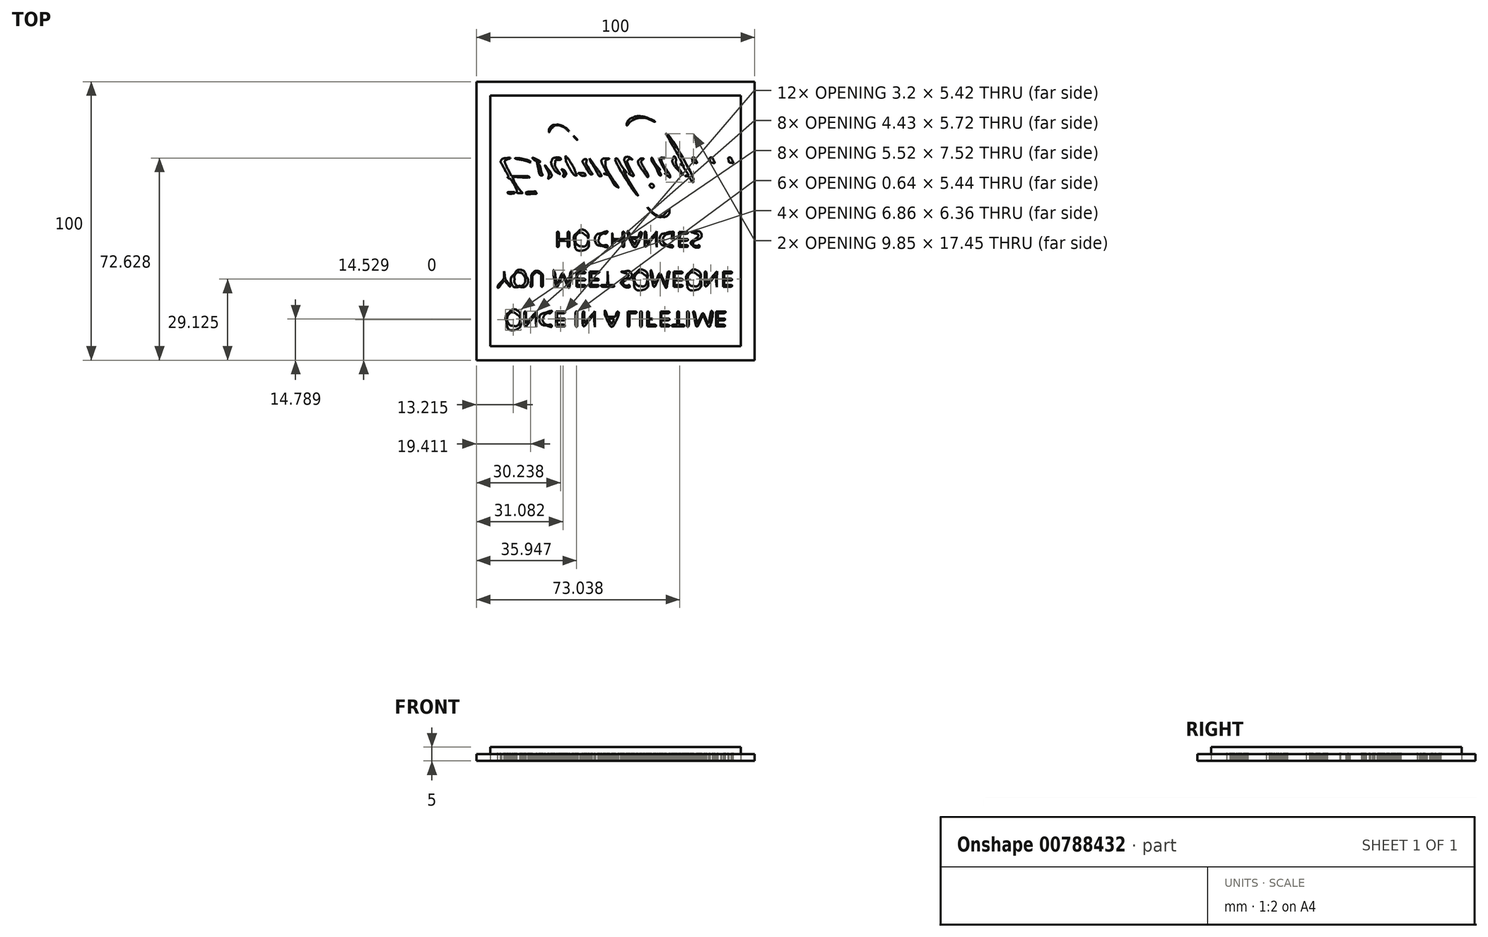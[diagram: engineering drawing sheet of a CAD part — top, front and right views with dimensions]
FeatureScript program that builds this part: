
annotation { "Feature Type Name" : "Feature", "Feature Type Description" : "" }
export const myFeature = defineFeature(function(context is Context, id is Id, definition is map)
    precondition{}
    {
        {
            var Q0;
            Q0=qCreatedBy(makeId("Top.planeOp"),FACE);
            var sketch = newSketch(context, id + "F0", { "sketchPlane" : qUnion([Q0])});
            skLineSegment(sketch, "E0.bottom", {"start": v(50, -50) * mm, "end": v(-50, -50) * mm});
            skLineSegment(sketch, "E0.top", {"start": v(50, 50) * mm, "end": v(-50, 50) * mm});
            skLineSegment(sketch, "E0.left", {"start": v(50, -50) * mm, "end": v(50, 50) * mm});
            skLineSegment(sketch, "E0.right", {"start": v(-50, -50) * mm, "end": v(-50, 50) * mm});
            skPoint(sketch, "E0.middle", {"position": v(0, 0) * mm});
            skSolve(sketch);
        }
        {
            var Q0;
            Q0=makeQuery(id+"F0.imprint","IMPRINT",FACE,{"disambiguationData":[TD([[makeQuery(id+"F0.imprint","IMPRINT",EDGE,{"derivedFrom":sQuery(id+"F0.wireOp",EDGE,"E0.bottom")}),-1.0]])]});
            var sketch = newSketch(context, id + "F1", { "sketchPlane" : qUnion([Q0])});
            skLineSegment(sketch, "E1.bottom", {"start": v(45, -45) * mm, "end": v(-45, -45) * mm});
            skLineSegment(sketch, "E1.top", {"start": v(45, 45) * mm, "end": v(-45, 45) * mm});
            skLineSegment(sketch, "E1.left", {"start": v(45, -45) * mm, "end": v(45, 45) * mm});
            skLineSegment(sketch, "E1.right", {"start": v(-45, -45) * mm, "end": v(-45, 45) * mm});
            skPoint(sketch, "E1.middle", {"position": v(0, 0) * mm});
            skSolve(sketch);
        }
        {
            var Q0;
            Q0 = qSketchRegion(id + "F0", true);
            extrude(context, id + "F2", {"entities" : qUnion([Q0]), "depth" : 2.5 * mm, "offsetDistance" : 25 * mm});
        }
        {
            var Q0;
            Q0 = qSketchRegion(id + "F1", true);
            extrude(context, id + "F3", {"entities" : qUnion([Q0]), "depth" : 5 * mm, "offsetDistance" : 25 * mm});
        }
        {
            var Q0;
            Q0=makeQuery(id+"F2.opExtrude","CAP_FACE",FACE,{"disambiguationData":[OSD([sQuery(id+"F0.wireOp",EDGE,"E0.bottom"),sQuery(id+"F0.wireOp",EDGE,"E0.top"),sQuery(id+"F0.wireOp",EDGE,"E0.left"),sQuery(id+"F0.wireOp",EDGE,"E0.right")])],"isStart":true});
            var sketch = newSketch(context, id + "F4", { "sketchPlane" : qUnion([Q0])});
            skFitSpline(sketch, "E2", {"points": [v(6.09, -37.09) * mm, v(5.28, -36.76) * mm, v(4.06, -35.27) * mm, v(4.06, -34.61) * mm]});
            skFitSpline(sketch, "E3", {"points": [v(4.06, -34.61) * mm, v(4.06, -34.31) * mm, v(4.31, -34.46) * mm, v(4.75, -35.01) * mm]});
            skFitSpline(sketch, "E4", {"points": [v(4.75, -35.01) * mm, v(5.13, -35.5) * mm, v(5.9, -36.08) * mm, v(6.49, -36.33) * mm]});
            skFitSpline(sketch, "E5", {"points": [v(6.49, -36.33) * mm, v(8.03, -36.97) * mm, v(11.26, -36.87) * mm, v(12.9, -36.13) * mm]});
            skFitSpline(sketch, "E6", {"points": [v(12.9, -36.13) * mm, v(13.64, -35.8) * mm, v(14.17, -35.64) * mm, v(14.08, -35.8) * mm]});
            skFitSpline(sketch, "E7", {"points": [v(14.08, -35.8) * mm, v(13.98, -35.96) * mm, v(13.1, -36.38) * mm, v(12.14, -36.74) * mm]});
            skFitSpline(sketch, "E8", {"points": [v(12.14, -36.74) * mm, v(10.33, -37.42) * mm, v(7.34, -37.6) * mm, v(6.09, -37.09) * mm]});
            skFitSpline(sketch, "E9", {"points": [v(15.82, -34.06) * mm, v(16.59, -33.28) * mm, v(17.3, -32.63) * mm, v(17.38, -32.63) * mm]});
            skFitSpline(sketch, "E10", {"points": [v(17.38, -32.63) * mm, v(17.47, -32.63) * mm, v(16.9, -33.28) * mm, v(16.13, -34.06) * mm]});
            skFitSpline(sketch, "E11", {"points": [v(16.13, -34.06) * mm, v(15.36, -34.85) * mm, v(14.66, -35.5) * mm, v(14.57, -35.5) * mm]});
            skFitSpline(sketch, "E12", {"points": [v(14.57, -35.5) * mm, v(14.49, -35.5) * mm, v(15.05, -34.85) * mm, v(15.82, -34.06) * mm]});
            skFitSpline(sketch, "E13", {"points": [v(-23.27, -33.9) * mm, v(-23.62, -33.55) * mm, v(-23.9, -32.95) * mm, v(-23.9, -32.55) * mm]});
            skFitSpline(sketch, "E14", {"points": [v(-23.9, -32.55) * mm, v(-23.88, -31.86) * mm, v(-23.87, -31.86) * mm, v(-23.54, -32.47) * mm]});
            skFitSpline(sketch, "E15", {"points": [v(-23.54, -32.47) * mm, v(-23.35, -32.82) * mm, v(-22.97, -33.29) * mm, v(-22.7, -33.5) * mm]});
            skFitSpline(sketch, "E16", {"points": [v(-22.7, -33.5) * mm, v(-21.6, -34.38) * mm, v(-18.62, -33.71) * mm, v(-16.92, -32.22) * mm]});
            skFitSpline(sketch, "E17", {"points": [v(-16.76, -32.28) * mm, v(-17.58, -33.27) * mm, v(-20.29, -34.53) * mm, v(-21.6, -34.54) * mm]});
            skFitSpline(sketch, "E18", {"points": [v(-21.6, -34.54) * mm, v(-22.21, -34.54) * mm, v(-22.9, -34.28) * mm, v(-23.27, -33.9) * mm]});
            skLineSegment(sketch, "E19", {"start": v(-16.92, -32.22) * mm, "end": v(-16.12, -31.52) * mm});
            skLineSegment(sketch, "E20", {"start": v(-16.12, -31.52) * mm, "end": v(-16.76, -32.28) * mm});
            skLineSegment(sketch, "E21", {"start": v(-16.76, -32.28) * mm, "end": v(-16.92, -32.22) * mm});
            skFitSpline(sketch, "E22", {"points": [v(18.46, -30.69) * mm, v(19.05, -29.76) * mm, v(24.08, -20.5) * mm, v(24.08, -20.32) * mm]});
            skFitSpline(sketch, "E23", {"points": [v(24.08, -20.32) * mm, v(24.08, -20.26) * mm, v(23.91, -20.3) * mm, v(23.71, -20.43) * mm]});
            skFitSpline(sketch, "E24", {"points": [v(23.71, -20.43) * mm, v(23.48, -20.57) * mm, v(23.43, -20.52) * mm, v(23.58, -20.28) * mm]});
            skFitSpline(sketch, "E25", {"points": [v(23.58, -20.28) * mm, v(23.7, -20.08) * mm, v(23.94, -20) * mm, v(24.1, -20.1) * mm]});
            skFitSpline(sketch, "E26", {"points": [v(24.1, -20.1) * mm, v(24.26, -20.2) * mm, v(24.4, -20.05) * mm, v(24.4, -19.76) * mm]});
            skFitSpline(sketch, "E27", {"points": [v(24.4, -19.76) * mm, v(24.4, -19.48) * mm, v(24.75, -18.73) * mm, v(25.2, -18.08) * mm]});
            skFitSpline(sketch, "E28", {"points": [v(25.2, -18.08) * mm, v(26.14, -16.7) * mm, v(26.16, -16.52) * mm, v(25.43, -16.33) * mm]});
            skFitSpline(sketch, "E29", {"points": [v(25.43, -16.33) * mm, v(25, -16.22) * mm, v(25.03, -16.17) * mm, v(25.57, -16.15) * mm]});
            skFitSpline(sketch, "E30", {"points": [v(25.57, -16.15) * mm, v(25.98, -16.12) * mm, v(26.5, -15.72) * mm, v(26.83, -15.16) * mm]});
            skFitSpline(sketch, "E31", {"points": [v(26.83, -15.16) * mm, v(27.43, -14.14) * mm, v(27.9, -13.92) * mm, v(27.9, -14.64) * mm]});
            skFitSpline(sketch, "E32", {"points": [v(27.9, -14.64) * mm, v(27.9, -15.5) * mm, v(19.06, -30.77) * mm, v(18.29, -31.25) * mm]});
            skFitSpline(sketch, "E33", {"points": [v(18.29, -31.25) * mm, v(18.12, -31.35) * mm, v(18.2, -31.1) * mm, v(18.46, -30.69) * mm]});
            skFitSpline(sketch, "E34", {"points": [v(-14.53, -29.77) * mm, v(-14.21, -29.42) * mm, v(-13.88, -29.14) * mm, v(-13.8, -29.14) * mm]});
            skFitSpline(sketch, "E35", {"points": [v(-13.8, -29.14) * mm, v(-13.7, -29.14) * mm, v(-13.9, -29.42) * mm, v(-14.21, -29.77) * mm]});
            skFitSpline(sketch, "E36", {"points": [v(-14.21, -29.77) * mm, v(-14.53, -30.12) * mm, v(-14.86, -30.4) * mm, v(-14.95, -30.4) * mm]});
            skFitSpline(sketch, "E37", {"points": [v(-14.95, -30.4) * mm, v(-15.03, -30.4) * mm, v(-14.85, -30.12) * mm, v(-14.53, -29.77) * mm]});
            skFitSpline(sketch, "E38", {"points": [v(-9.92, -23.1) * mm, v(-9.74, -22.75) * mm, v(-9.51, -22.46) * mm, v(-9.42, -22.46) * mm]});
            skFitSpline(sketch, "E39", {"points": [v(-9.42, -22.46) * mm, v(-9.34, -22.46) * mm, v(-9.42, -22.75) * mm, v(-9.6, -23.1) * mm]});
            skFitSpline(sketch, "E40", {"points": [v(-9.6, -23.1) * mm, v(-9.8, -23.45) * mm, v(-10.02, -23.74) * mm, v(-10.1, -23.74) * mm]});
            skFitSpline(sketch, "E41", {"points": [v(-10.1, -23.74) * mm, v(-10.2, -23.74) * mm, v(-10.1, -23.45) * mm, v(-9.92, -23.1) * mm]});
            skFitSpline(sketch, "E42", {"points": [v(-39.71, -22.55) * mm, v(-40.28, -22.48) * mm, v(-40.88, -22.17) * mm, v(-41.05, -21.86) * mm]});
            skFitSpline(sketch, "E43", {"points": [v(-41.05, -21.86) * mm, v(-41.37, -21.26) * mm, v(-41.32, -21.14) * mm, v(-39.5, -17.95) * mm]});
            skFitSpline(sketch, "E44", {"points": [v(-39.5, -17.95) * mm, v(-38.94, -16.95) * mm, v(-38.55, -16) * mm, v(-38.65, -15.83) * mm]});
            skFitSpline(sketch, "E45", {"points": [v(-38.65, -15.83) * mm, v(-38.75, -15.67) * mm, v(-38.64, -15.46) * mm, v(-38.4, -15.37) * mm]});
            skFitSpline(sketch, "E46", {"points": [v(-38.4, -15.37) * mm, v(-37.92, -15.19) * mm, v(-35.56, -11.12) * mm, v(-35.56, -10.48) * mm]});
            skFitSpline(sketch, "E47", {"points": [v(-35.56, -10.48) * mm, v(-35.56, -10.23) * mm, v(-35.15, -10.07) * mm, v(-34.48, -10.07) * mm]});
            skFitSpline(sketch, "E48", {"points": [v(-34.48, -10.07) * mm, v(-33.44, -10.07) * mm, v(-33.43, -10.09) * mm, v(-33.98, -10.68) * mm]});
            skFitSpline(sketch, "E49", {"points": [v(-33.98, -10.68) * mm, v(-34.63, -11.38) * mm, v(-36.47, -14.37) * mm, v(-36.81, -15.29) * mm]});
            skFitSpline(sketch, "E50", {"points": [v(-36.81, -15.29) * mm, v(-37.03, -15.87) * mm, v(-36.9, -15.88) * mm, v(-33.95, -15.7) * mm]});
            skFitSpline(sketch, "E51", {"points": [v(-33.95, -15.7) * mm, v(-31.98, -15.56) * mm, v(-30.94, -15.6) * mm, v(-31.06, -15.8) * mm]});
            skFitSpline(sketch, "E52", {"points": [v(-31.06, -15.8) * mm, v(-31.16, -15.97) * mm, v(-32.64, -16.1) * mm, v(-34.34, -16.1) * mm]});
            skFitSpline(sketch, "E53", {"points": [v(-38.45, -18.18) * mm, v(-39.52, -20.34) * mm, v(-39.74, -21.63) * mm, v(-39.1, -22.02) * mm]});
            skFitSpline(sketch, "E54", {"points": [v(-39.1, -22.02) * mm, v(-38.9, -22.14) * mm, v(-38.3, -22.35) * mm, v(-37.75, -22.48) * mm]});
            skLineSegment(sketch, "E55", {"start": v(-34.34, -16.1) * mm, "end": v(-37.43, -16.1) * mm});
            skLineSegment(sketch, "E56", {"start": v(-37.43, -16.1) * mm, "end": v(-38.45, -18.18) * mm});
            skLineSegment(sketch, "E57", {"start": v(-38.45, -18.18) * mm, "end": v(-34.34, -16.1) * mm});
            skFitSpline(sketch, "E58", {"points": [v(-37.73, -22.7) * mm, v(-38.25, -22.69) * mm, v(-39.14, -22.62) * mm, v(-39.71, -22.55) * mm]});
            skLineSegment(sketch, "E59", {"start": v(-37.75, -22.48) * mm, "end": v(-36.77, -22.72) * mm});
            skLineSegment(sketch, "E60", {"start": v(-36.77, -22.72) * mm, "end": v(-37.73, -22.7) * mm});
            skLineSegment(sketch, "E61", {"start": v(-37.73, -22.7) * mm, "end": v(-37.75, -22.48) * mm});
            skFitSpline(sketch, "E62", {"points": [v(3.22, -22.3) * mm, v(3.12, -22.04) * mm, v(3.55, -20.75) * mm, v(4.17, -19.44) * mm]});
            skFitSpline(sketch, "E63", {"points": [v(4.17, -19.44) * mm, v(4.86, -17.99) * mm, v(5.15, -17.06) * mm, v(4.92, -17.05) * mm]});
            skFitSpline(sketch, "E64", {"points": [v(4.92, -17.05) * mm, v(4.7, -17.04) * mm, v(4.94, -16.82) * mm, v(5.44, -16.55) * mm]});
            skFitSpline(sketch, "E65", {"points": [v(5.44, -16.55) * mm, v(5.93, -16.28) * mm, v(6.41, -16.13) * mm, v(6.5, -16.22) * mm]});
            skFitSpline(sketch, "E66", {"points": [v(6.5, -16.22) * mm, v(6.59, -16.3) * mm, v(6.3, -17) * mm, v(5.85, -17.75) * mm]});
            skFitSpline(sketch, "E67", {"points": [v(5.85, -17.75) * mm, v(5.4, -18.5) * mm, v(4.83, -19.66) * mm, v(4.56, -20.3) * mm]});
            skFitSpline(sketch, "E68", {"points": [v(4.56, -20.3) * mm, v(4.12, -21.35) * mm, v(4.12, -21.52) * mm, v(4.55, -21.95) * mm]});
            skFitSpline(sketch, "E69", {"points": [v(4.55, -21.95) * mm, v(4.81, -22.22) * mm, v(5.28, -22.36) * mm, v(5.58, -22.26) * mm]});
            skFitSpline(sketch, "E70", {"points": [v(5.58, -22.26) * mm, v(6.04, -22.11) * mm, v(6.05, -22.14) * mm, v(5.65, -22.43) * mm]});
            skFitSpline(sketch, "E71", {"points": [v(5.65, -22.43) * mm, v(4.94, -22.94) * mm, v(3.43, -22.86) * mm, v(3.22, -22.3) * mm]});
            skLineSegment(sketch, "E72", {"start": v(-39.71, -22.55) * mm, "end": v(-39.71, -22.55) * mm});
            skFitSpline(sketch, "E73", {"points": [v(15.93, -22.31) * mm, v(15.83, -22.05) * mm, v(16.34, -20.76) * mm, v(17.06, -19.45) * mm]});
            skFitSpline(sketch, "E74", {"points": [v(17.06, -19.45) * mm, v(17.84, -18.03) * mm, v(18.22, -17.06) * mm, v(17.98, -17.06) * mm]});
            skFitSpline(sketch, "E75", {"points": [v(17.98, -17.06) * mm, v(17.76, -17.06) * mm, v(17.9, -16.84) * mm, v(18.3, -16.56) * mm]});
            skFitSpline(sketch, "E76", {"points": [v(18.3, -16.56) * mm, v(19.58, -15.66) * mm, v(19.6, -16.23) * mm, v(18.34, -18.34) * mm]});
            skFitSpline(sketch, "E77", {"points": [v(18.34, -18.34) * mm, v(16.8, -20.9) * mm, v(16.45, -22.34) * mm, v(17.3, -22.56) * mm]});
            skFitSpline(sketch, "E78", {"points": [v(17.3, -22.56) * mm, v(17.7, -22.66) * mm, v(17.6, -22.72) * mm, v(17, -22.74) * mm]});
            skFitSpline(sketch, "E79", {"points": [v(17, -22.74) * mm, v(16.48, -22.77) * mm, v(16.04, -22.59) * mm, v(15.93, -22.31) * mm]});
            skFitSpline(sketch, "E80", {"points": [v(20.71, -22.34) * mm, v(20.38, -21.49) * mm, v(21.18, -19.8) * mm, v(22.67, -18.16) * mm]});
            skFitSpline(sketch, "E81", {"points": [v(22.67, -18.16) * mm, v(24.2, -16.5) * mm, v(24.2, -16.68) * mm, v(22.68, -18.9) * mm]});
            skFitSpline(sketch, "E82", {"points": [v(22.68, -18.9) * mm, v(22.15, -19.69) * mm, v(21.73, -20.76) * mm, v(21.68, -21.43) * mm]});
            skFitSpline(sketch, "E83", {"points": [v(21.68, -21.43) * mm, v(21.61, -22.65) * mm, v(21.04, -23.19) * mm, v(20.71, -22.34) * mm]});
            skFitSpline(sketch, "E84", {"points": [v(-33.87, -21.99) * mm, v(-32.8, -21.76) * mm, v(-31.44, -21.32) * mm, v(-30.85, -21.03) * mm]});
            skFitSpline(sketch, "E85", {"points": [v(-30.42, -21.15) * mm, v(-30.78, -21.53) * mm, v(-31.8, -21.95) * mm, v(-32.77, -22.14) * mm]});
            skFitSpline(sketch, "E86", {"points": [v(-32.77, -22.14) * mm, v(-35.26, -22.61) * mm, v(-36.16, -22.49) * mm, v(-33.87, -21.99) * mm]});
            skLineSegment(sketch, "E87", {"start": v(-30.85, -21.03) * mm, "end": v(-29.78, -20.5) * mm});
            skLineSegment(sketch, "E88", {"start": v(-29.78, -20.5) * mm, "end": v(-30.42, -21.15) * mm});
            skLineSegment(sketch, "E89", {"start": v(-30.42, -21.15) * mm, "end": v(-30.85, -21.03) * mm});
            skFitSpline(sketch, "E90", {"points": [v(-29.43, -22.14) * mm, v(-29.1, -21.8) * mm, v(-27.08, -21.14) * mm, v(-27.08, -21.37) * mm]});
            skFitSpline(sketch, "E91", {"points": [v(-27.08, -21.37) * mm, v(-27.08, -21.44) * mm, v(-27.5, -21.71) * mm, v(-28.02, -21.98) * mm]});
            skFitSpline(sketch, "E92", {"points": [v(-28.02, -21.98) * mm, v(-29.11, -22.54) * mm, v(-29.92, -22.64) * mm, v(-29.43, -22.14) * mm]});
            skFitSpline(sketch, "E93", {"points": [v(-22.74, -22) * mm, v(-23.14, -20.98) * mm, v(-21.65, -17.9) * mm, v(-20.36, -17.1) * mm]});
            skFitSpline(sketch, "E94", {"points": [v(-20.36, -17.1) * mm, v(-19.94, -16.84) * mm, v(-20, -17.04) * mm, v(-20.59, -17.92) * mm]});
            skFitSpline(sketch, "E95", {"points": [v(-20.59, -17.92) * mm, v(-21.49, -19.25) * mm, v(-21.78, -20.17) * mm, v(-21.63, -21.24) * mm]});
            skFitSpline(sketch, "E96", {"points": [v(-21.63, -21.24) * mm, v(-21.54, -21.84) * mm, v(-21.33, -21.99) * mm, v(-20.52, -21.99) * mm]});
            skFitSpline(sketch, "E97", {"points": [v(-20.52, -21.99) * mm, v(-19.97, -21.99) * mm, v(-19.58, -22.1) * mm, v(-19.66, -22.22) * mm]});
            skFitSpline(sketch, "E98", {"points": [v(-19.66, -22.22) * mm, v(-19.94, -22.68) * mm, v(-22.55, -22.5) * mm, v(-22.74, -22) * mm]});
            skFitSpline(sketch, "E99", {"points": [v(-17.85, -22.23) * mm, v(-17.8, -21.54) * mm, v(-14.72, -16.43) * mm, v(-14.35, -16.43) * mm]});
            skFitSpline(sketch, "E100", {"points": [v(-14.35, -16.43) * mm, v(-13.97, -16.43) * mm, v(-13.98, -16.5) * mm, v(-14.45, -17.58) * mm]});
            skFitSpline(sketch, "E101", {"points": [v(-14.45, -17.58) * mm, v(-15.5, -19.98) * mm, v(-17.92, -23.29) * mm, v(-17.85, -22.23) * mm]});
            skFitSpline(sketch, "E102", {"points": [v(-4.63, -22.25) * mm, v(-5.07, -21.8) * mm, v(-4.8, -20.56) * mm, v(-3.9, -18.84) * mm]});
            skFitSpline(sketch, "E103", {"points": [v(-3.9, -18.84) * mm, v(-2.97, -17.08) * mm, v(-2.97, -17.06) * mm, v(-3.66, -17.03) * mm]});
            skFitSpline(sketch, "E104", {"points": [v(-3.66, -17.03) * mm, v(-4.22, -17.01) * mm, v(-4.17, -16.95) * mm, v(-3.4, -16.72) * mm]});
            skFitSpline(sketch, "E105", {"points": [v(-3.4, -16.72) * mm, v(-2.7, -16.51) * mm, v(-2.17, -15.94) * mm, v(-1.38, -14.56) * mm]});
            skFitSpline(sketch, "E106", {"points": [v(-1.38, -14.56) * mm, v(-0.78, -13.52) * mm, v(0.04, -12.52) * mm, v(0.44, -12.34) * mm]});
            skFitSpline(sketch, "E107", {"points": [v(0.44, -12.34) * mm, v(1.12, -12.03) * mm, v(1.1, -12.13) * mm, v(0.12, -13.5) * mm]});
            skFitSpline(sketch, "E108", {"points": [v(0.12, -13.5) * mm, v(-1.72, -16.1) * mm, v(-3.57, -19.76) * mm, v(-3.57, -20.83) * mm]});
            skFitSpline(sketch, "E109", {"points": [v(-3.57, -20.83) * mm, v(-3.57, -21.59) * mm, v(-3.38, -21.92) * mm, v(-2.85, -22.14) * mm]});
            skFitSpline(sketch, "E110", {"points": [v(-2.85, -22.14) * mm, v(-2.22, -22.39) * mm, v(-2.27, -22.43) * mm, v(-3.28, -22.44) * mm]});
            skFitSpline(sketch, "E111", {"points": [v(-3.28, -22.44) * mm, v(-3.9, -22.45) * mm, v(-4.5, -22.37) * mm, v(-4.63, -22.25) * mm]});
            skFitSpline(sketch, "E112", {"points": [v(-0.07, -22.28) * mm, v(-0.07, -21.75) * mm, v(7.4, -9.56) * mm, v(7.93, -9.24) * mm]});
            skFitSpline(sketch, "E113", {"points": [v(7.93, -9.24) * mm, v(8.09, -9.14) * mm, v(7.73, -9.83) * mm, v(7.13, -10.76) * mm]});
            skFitSpline(sketch, "E114", {"points": [v(7.13, -10.76) * mm, v(5.14, -13.88) * mm, v(2.94, -18.2) * mm, v(3.6, -17.7) * mm]});
            skFitSpline(sketch, "E115", {"points": [v(3.6, -17.7) * mm, v(3.94, -17.44) * mm, v(3.79, -17.72) * mm, v(3.27, -18.34) * mm]});
            skFitSpline(sketch, "E116", {"points": [v(3.27, -18.34) * mm, v(2.74, -18.95) * mm, v(1.95, -20.13) * mm, v(1.52, -20.96) * mm]});
            skFitSpline(sketch, "E117", {"points": [v(1.52, -20.96) * mm, v(1.08, -21.79) * mm, v(0.55, -22.46) * mm, v(0.33, -22.46) * mm]});
            skFitSpline(sketch, "E118", {"points": [v(0.33, -22.46) * mm, v(0.1, -22.46) * mm, v(-0.07, -22.38) * mm, v(-0.07, -22.28) * mm]});
            skLineSegment(sketch, "E119", {"start": v(-4.63, -22.25) * mm, "end": v(-4.63, -22.25) * mm});
            skFitSpline(sketch, "E120", {"points": [v(8.52, -22) * mm, v(8.08, -21.47) * mm, v(8.95, -19.23) * mm, v(10.28, -17.48) * mm]});
            skFitSpline(sketch, "E121", {"points": [v(10.28, -17.48) * mm, v(11.6, -15.75) * mm, v(11.75, -16.28) * mm, v(10.57, -18.44) * mm]});
            skFitSpline(sketch, "E122", {"points": [v(10.57, -18.44) * mm, v(9.4, -20.57) * mm, v(9.22, -21.46) * mm, v(9.84, -22.08) * mm]});
            skFitSpline(sketch, "E123", {"points": [v(9.84, -22.08) * mm, v(10.14, -22.38) * mm, v(10.08, -22.46) * mm, v(9.56, -22.46) * mm]});
            skFitSpline(sketch, "E124", {"points": [v(9.56, -22.46) * mm, v(9.2, -22.46) * mm, v(8.73, -22.26) * mm, v(8.52, -22) * mm]});
            skFitSpline(sketch, "E125", {"points": [v(12.96, -22) * mm, v(12.96, -21.75) * mm, v(13.3, -21.03) * mm, v(13.72, -20.42) * mm]});
            skFitSpline(sketch, "E126", {"points": [v(13.72, -20.42) * mm, v(14.14, -19.8) * mm, v(14.74, -18.65) * mm, v(15.07, -17.86) * mm]});
            skFitSpline(sketch, "E127", {"points": [v(15.07, -17.86) * mm, v(15.4, -17.07) * mm, v(15.84, -16.43) * mm, v(16.06, -16.43) * mm]});
            skFitSpline(sketch, "E128", {"points": [v(16.06, -16.43) * mm, v(16.34, -16.43) * mm, v(16.26, -16.83) * mm, v(15.78, -17.77) * mm]});
            skFitSpline(sketch, "E129", {"points": [v(15.78, -17.77) * mm, v(15.15, -19) * mm, v(15.14, -19.08) * mm, v(15.7, -18.65) * mm]});
            skFitSpline(sketch, "E130", {"points": [v(15.7, -18.65) * mm, v(16.02, -18.39) * mm, v(15.83, -18.71) * mm, v(15.27, -19.37) * mm]});
            skFitSpline(sketch, "E131", {"points": [v(15.27, -19.37) * mm, v(14.7, -20.03) * mm, v(14.02, -21) * mm, v(13.75, -21.51) * mm]});
            skFitSpline(sketch, "E132", {"points": [v(13.75, -21.51) * mm, v(13.21, -22.56) * mm, v(12.96, -22.71) * mm, v(12.96, -22) * mm]});
            skFitSpline(sketch, "E133", {"points": [v(27.63, -21.75) * mm, v(27.7, -21.29) * mm, v(27.99, -21) * mm, v(28.45, -20.93) * mm]});
            skFitSpline(sketch, "E134", {"points": [v(28.45, -20.93) * mm, v(29.25, -20.82) * mm, v(29.3, -20.96) * mm, v(28.83, -21.85) * mm]});
            skFitSpline(sketch, "E135", {"points": [v(28.83, -21.85) * mm, v(28.37, -22.72) * mm, v(27.5, -22.65) * mm, v(27.63, -21.75) * mm]});
            skFitSpline(sketch, "E136", {"points": [v(33.99, -21.75) * mm, v(34.05, -21.29) * mm, v(34.34, -21) * mm, v(34.8, -20.93) * mm]});
            skFitSpline(sketch, "E137", {"points": [v(34.8, -20.93) * mm, v(35.6, -20.82) * mm, v(35.67, -20.96) * mm, v(35.19, -21.85) * mm]});
            skFitSpline(sketch, "E138", {"points": [v(35.19, -21.85) * mm, v(34.72, -22.72) * mm, v(33.86, -22.65) * mm, v(33.99, -21.75) * mm]});
            skFitSpline(sketch, "E139", {"points": [v(40.66, -21.75) * mm, v(40.73, -21.29) * mm, v(41.02, -21) * mm, v(41.48, -20.93) * mm]});
            skFitSpline(sketch, "E140", {"points": [v(41.48, -20.93) * mm, v(42.28, -20.82) * mm, v(42.34, -20.96) * mm, v(41.86, -21.85) * mm]});
            skFitSpline(sketch, "E141", {"points": [v(41.86, -21.85) * mm, v(41.4, -22.72) * mm, v(40.53, -22.65) * mm, v(40.66, -21.75) * mm]});
            skFitSpline(sketch, "E142", {"points": [v(-11.65, -21.86) * mm, v(-11.9, -21.45) * mm, v(-11.59, -20.68) * mm, v(-10.3, -18.57) * mm]});
            skFitSpline(sketch, "E143", {"points": [v(-10.3, -18.57) * mm, v(-9.7, -17.57) * mm, v(-9, -16.74) * mm, v(-8.74, -16.74) * mm]});
            skFitSpline(sketch, "E144", {"points": [v(-8.74, -16.74) * mm, v(-8.29, -16.74) * mm, v(-8.5, -17.18) * mm, v(-10.18, -19.84) * mm]});
            skFitSpline(sketch, "E145", {"points": [v(-10.18, -19.84) * mm, v(-10.43, -20.24) * mm, v(-10.56, -20.92) * mm, v(-10.48, -21.35) * mm]});
            skFitSpline(sketch, "E146", {"points": [v(-10.48, -21.35) * mm, v(-10.36, -21.96) * mm, v(-10.46, -22.15) * mm, v(-10.9, -22.15) * mm]});
            skFitSpline(sketch, "E147", {"points": [v(-10.9, -22.15) * mm, v(-11.22, -22.15) * mm, v(-11.55, -22.02) * mm, v(-11.65, -21.86) * mm]});
            skFitSpline(sketch, "E148", {"points": [v(-9.1, -21.67) * mm, v(-8.97, -21.32) * mm, v(-8.7, -20.82) * mm, v(-8.5, -20.56) * mm]});
            skFitSpline(sketch, "E149", {"points": [v(-8.5, -20.56) * mm, v(-8.28, -20.3) * mm, v(-7.63, -19.19) * mm, v(-7.04, -18.1) * mm]});
            skFitSpline(sketch, "E150", {"points": [v(-7.04, -18.1) * mm, v(-6.45, -17) * mm, v(-5.85, -16.1) * mm, v(-5.72, -16.1) * mm]});
            skFitSpline(sketch, "E151", {"points": [v(-5.72, -16.1) * mm, v(-5.1, -16.1) * mm, v(-5.61, -17.34) * mm, v(-7.12, -19.4) * mm]});
            skFitSpline(sketch, "E152", {"points": [v(-7.12, -19.4) * mm, v(-9.17, -22.23) * mm, v(-9.38, -22.47) * mm, v(-9.1, -21.67) * mm]});
            skFitSpline(sketch, "E153", {"points": [v(-27.84, -19.14) * mm, v(-27.42, -17.13) * mm, v(-27.05, -16.44) * mm, v(-26.36, -16.43) * mm]});
            skFitSpline(sketch, "E154", {"points": [v(-26.36, -16.43) * mm, v(-26.22, -16.43) * mm, v(-26.24, -16.68) * mm, v(-26.4, -16.98) * mm]});
            skFitSpline(sketch, "E155", {"points": [v(-26.4, -16.98) * mm, v(-26.55, -17.29) * mm, v(-26.78, -18.06) * mm, v(-26.9, -18.7) * mm]});
            skFitSpline(sketch, "E156", {"points": [v(-26.9, -18.7) * mm, v(-27, -19.35) * mm, v(-27.37, -20.2) * mm, v(-27.7, -20.61) * mm]});
            skFitSpline(sketch, "E157", {"points": [v(-27.7, -20.61) * mm, v(-28.3, -21.34) * mm, v(-28.3, -21.32) * mm, v(-27.84, -19.14) * mm]});
            skFitSpline(sketch, "E158", {"points": [v(-24.64, -18.41) * mm, v(-24.12, -17.4) * mm, v(-23.92, -16.6) * mm, v(-24.04, -16) * mm]});
            skFitSpline(sketch, "E159", {"points": [v(-24.04, -16) * mm, v(-24.2, -15.2) * mm, v(-24.15, -15.13) * mm, v(-23.74, -15.47) * mm]});
            skFitSpline(sketch, "E160", {"points": [v(-23.74, -15.47) * mm, v(-23.01, -16.08) * mm, v(-23.18, -17.16) * mm, v(-24.22, -18.6) * mm]});
            skFitSpline(sketch, "E161", {"points": [v(-24.22, -18.6) * mm, v(-24.75, -19.33) * mm, v(-25.23, -19.92) * mm, v(-25.3, -19.92) * mm]});
            skFitSpline(sketch, "E162", {"points": [v(-25.3, -19.92) * mm, v(-25.36, -19.92) * mm, v(-25.06, -19.24) * mm, v(-24.64, -18.41) * mm]});
            skFitSpline(sketch, "E163", {"points": [v(-18.97, -17.9) * mm, v(-18.7, -17.48) * mm, v(-18.58, -16.92) * mm, v(-18.69, -16.63) * mm]});
            skFitSpline(sketch, "E164", {"points": [v(-18.69, -16.63) * mm, v(-18.9, -16.05) * mm, v(-18.35, -15.9) * mm, v(-18, -16.46) * mm]});
            skFitSpline(sketch, "E165", {"points": [v(-18, -16.46) * mm, v(-17.74, -16.88) * mm, v(-18.43, -18.24) * mm, v(-19.02, -18.47) * mm]});
            skFitSpline(sketch, "E166", {"points": [v(-19.02, -18.47) * mm, v(-19.36, -18.6) * mm, v(-19.35, -18.47) * mm, v(-18.97, -17.9) * mm]});
            skFitSpline(sketch, "E167", {"points": [v(-12.89, -16.82) * mm, v(-12.17, -16.3) * mm, v(-10.78, -16.3) * mm, v(-10.95, -16.82) * mm]});
            skFitSpline(sketch, "E168", {"points": [v(-10.95, -16.82) * mm, v(-11.03, -17.04) * mm, v(-11.61, -17.22) * mm, v(-12.26, -17.22) * mm]});
            skFitSpline(sketch, "E169", {"points": [v(-12.26, -17.22) * mm, v(-13.27, -17.22) * mm, v(-13.36, -17.17) * mm, v(-12.89, -16.82) * mm]});
            skFitSpline(sketch, "E170", {"points": [v(12.32, -12.97) * mm, v(12.32, -12.57) * mm, v(13.25, -11.85) * mm, v(13.48, -12.08) * mm]});
            skFitSpline(sketch, "E171", {"points": [v(13.48, -12.08) * mm, v(13.8, -12.4) * mm, v(13.32, -13.25) * mm, v(12.8, -13.25) * mm]});
            skFitSpline(sketch, "E172", {"points": [v(12.8, -13.25) * mm, v(12.54, -13.25) * mm, v(12.32, -13.12) * mm, v(12.32, -12.97) * mm]});
            skLineSegment(sketch, "E173", {"start": v(-12.89, -16.82) * mm, "end": v(-12.89, -16.82) * mm});
            skFitSpline(sketch, "E174", {"points": [v(-30.26, -10.47) * mm, v(-32.18, -10.25) * mm, v(-32.12, -9.75) * mm, v(-30.17, -9.75) * mm]});
            skFitSpline(sketch, "E175", {"points": [v(-30.17, -9.75) * mm, v(-28.7, -9.75) * mm, v(-28.4, -9.84) * mm, v(-28.56, -10.23) * mm]});
            skFitSpline(sketch, "E176", {"points": [v(-28.56, -10.23) * mm, v(-28.66, -10.5) * mm, v(-28.83, -10.68) * mm, v(-28.94, -10.66) * mm]});
            skFitSpline(sketch, "E177", {"points": [v(-28.94, -10.66) * mm, v(-29.06, -10.63) * mm, v(-29.65, -10.55) * mm, v(-30.26, -10.47) * mm]});
            skFitSpline(sketch, "E178", {"points": [v(-38.72, -10.13) * mm, v(-38.57, -9.89) * mm, v(-36.3, -10.01) * mm, v(-36.3, -10.26) * mm]});
            skFitSpline(sketch, "E179", {"points": [v(-36.3, -10.26) * mm, v(-36.3, -10.33) * mm, v(-36.88, -10.39) * mm, v(-37.59, -10.39) * mm]});
            skFitSpline(sketch, "E180", {"points": [v(-37.59, -10.39) * mm, v(-38.3, -10.39) * mm, v(-38.8, -10.27) * mm, v(-38.72, -10.13) * mm]});
            skFitSpline(sketch, "E181", {"points": [v(11.53, -4.7) * mm, v(13.5, -2.61) * mm, v(15.34, -1.51) * mm, v(16.86, -1.5) * mm]});
            skFitSpline(sketch, "E182", {"points": [v(16.86, -1.5) * mm, v(17.9, -1.5) * mm, v(19.31, -2.75) * mm, v(19.31, -3.68) * mm]});
            skFitSpline(sketch, "E183", {"points": [v(19.31, -3.68) * mm, v(19.31, -4.23) * mm, v(19.2, -4.2) * mm, v(18.38, -3.37) * mm]});
            skFitSpline(sketch, "E184", {"points": [v(18.38, -3.37) * mm, v(16.77, -1.76) * mm, v(14.38, -2.3) * mm, v(11.55, -4.93) * mm]});
            skFitSpline(sketch, "E185", {"points": [v(-28.51, 4.3) * mm, v(-28.59, 4.53) * mm, v(-29, 5.67) * mm, v(-29.42, 6.85) * mm]});
            skFitSpline(sketch, "E186", {"points": [v(-29.42, 6.85) * mm, v(-29.84, 8.04) * mm, v(-30.06, 9.08) * mm, v(-29.9, 9.18) * mm]});
            skFitSpline(sketch, "E187", {"points": [v(-29.9, 9.18) * mm, v(-29.6, 9.36) * mm, v(-29.32, 8.74) * mm, v(-28.65, 6.51) * mm]});
            skFitSpline(sketch, "E188", {"points": [v(-28.65, 6.51) * mm, v(-28.43, 5.78) * mm, v(-28.17, 5.18) * mm, v(-28.06, 5.18) * mm]});
            skFitSpline(sketch, "E189", {"points": [v(-28.06, 5.18) * mm, v(-27.96, 5.18) * mm, v(-27.58, 6) * mm, v(-27.22, 6.99) * mm]});
            skFitSpline(sketch, "E190", {"points": [v(-27.22, 6.99) * mm, v(-26.87, 7.98) * mm, v(-26.42, 8.85) * mm, v(-26.22, 8.91) * mm]});
            skFitSpline(sketch, "E191", {"points": [v(-26.22, 8.91) * mm, v(-26.03, 8.97) * mm, v(-25.63, 8.27) * mm, v(-25.33, 7.34) * mm]});
            skFitSpline(sketch, "E192", {"points": [v(-25.33, 7.34) * mm, v(-25.03, 6.42) * mm, v(-24.67, 5.54) * mm, v(-24.54, 5.4) * mm]});
            skFitSpline(sketch, "E193", {"points": [v(-24.54, 5.4) * mm, v(-24.4, 5.25) * mm, v(-23.98, 6.07) * mm, v(-23.6, 7.22) * mm]});
            skFitSpline(sketch, "E194", {"points": [v(-23.6, 7.22) * mm, v(-23.21, 8.37) * mm, v(-22.77, 9.31) * mm, v(-22.6, 9.31) * mm]});
            skFitSpline(sketch, "E195", {"points": [v(-22.6, 9.31) * mm, v(-22.22, 9.31) * mm, v(-22.19, 9.47) * mm, v(-23.23, 6.6) * mm]});
            skFitSpline(sketch, "E196", {"points": [v(-23.23, 6.6) * mm, v(-23.73, 5.23) * mm, v(-24.28, 4.05) * mm, v(-24.45, 4) * mm]});
            skFitSpline(sketch, "E197", {"points": [v(-24.45, 4) * mm, v(-24.62, 3.94) * mm, v(-25.01, 4.76) * mm, v(-25.34, 5.82) * mm]});
            skFitSpline(sketch, "E198", {"points": [v(-25.34, 5.82) * mm, v(-25.66, 6.89) * mm, v(-26.03, 7.82) * mm, v(-26.15, 7.9) * mm]});
            skFitSpline(sketch, "E199", {"points": [v(-26.15, 7.9) * mm, v(-26.28, 7.98) * mm, v(-26.72, 7.11) * mm, v(-27.13, 5.98) * mm]});
            skFitSpline(sketch, "E200", {"points": [v(-27.13, 5.98) * mm, v(-27.85, 3.96) * mm, v(-28.23, 3.5) * mm, v(-28.51, 4.3) * mm]});
            skLineSegment(sketch, "E201", {"start": v(11.55, -4.93) * mm, "end": v(9.62, -6.71) * mm});
            skLineSegment(sketch, "E202", {"start": v(9.62, -6.71) * mm, "end": v(11.53, -4.7) * mm});
            skLineSegment(sketch, "E203", {"start": v(11.53, -4.7) * mm, "end": v(11.55, -4.93) * mm});
            skFitSpline(sketch, "E204", {"points": [v(-21.04, 6.61) * mm, v(-21.04, 8.2) * mm, v(-20.91, 9.31) * mm, v(-20.73, 9.31) * mm]});
            skFitSpline(sketch, "E205", {"points": [v(-20.73, 9.31) * mm, v(-20.55, 9.31) * mm, v(-20.4, 8.81) * mm, v(-20.4, 8.2) * mm]});
            skFitSpline(sketch, "E206", {"points": [v(-17.23, 8.2) * mm, v(-17.23, 8.81) * mm, v(-17.09, 9.31) * mm, v(-16.91, 9.31) * mm]});
            skFitSpline(sketch, "E207", {"points": [v(-16.91, 9.31) * mm, v(-16.73, 9.31) * mm, v(-16.6, 8.2) * mm, v(-16.6, 6.61) * mm]});
            skFitSpline(sketch, "E208", {"points": [v(-16.6, 6.61) * mm, v(-16.6, 5.02) * mm, v(-16.73, 3.91) * mm, v(-16.91, 3.91) * mm]});
            skFitSpline(sketch, "E209", {"points": [v(-16.91, 3.91) * mm, v(-17.09, 3.91) * mm, v(-17.23, 4.48) * mm, v(-17.23, 5.18) * mm]});
            skLineSegment(sketch, "E210", {"start": v(-20.4, 8.2) * mm, "end": v(-20.4, 7.09) * mm});
            skLineSegment(sketch, "E211", {"start": v(-20.4, 7.09) * mm, "end": v(-18.82, 7.09) * mm});
            skLineSegment(sketch, "E212", {"start": v(-18.82, 7.09) * mm, "end": v(-17.23, 7.09) * mm});
            skLineSegment(sketch, "E213", {"start": v(-17.23, 7.09) * mm, "end": v(-17.23, 8.2) * mm});
            skLineSegment(sketch, "E214", {"start": v(-17.23, 8.2) * mm, "end": v(-20.4, 8.2) * mm});
            skFitSpline(sketch, "E215", {"points": [v(-20.4, 5.18) * mm, v(-20.4, 4.48) * mm, v(-20.55, 3.91) * mm, v(-20.73, 3.91) * mm]});
            skFitSpline(sketch, "E216", {"points": [v(-20.73, 3.91) * mm, v(-20.91, 3.91) * mm, v(-21.04, 5.02) * mm, v(-21.04, 6.61) * mm]});
            skLineSegment(sketch, "E217", {"start": v(-17.23, 5.18) * mm, "end": v(-17.23, 6.45) * mm});
            skLineSegment(sketch, "E218", {"start": v(-17.23, 6.45) * mm, "end": v(-18.82, 6.45) * mm});
            skLineSegment(sketch, "E219", {"start": v(-18.82, 6.45) * mm, "end": v(-20.4, 6.45) * mm});
            skLineSegment(sketch, "E220", {"start": v(-20.4, 6.45) * mm, "end": v(-20.4, 5.18) * mm});
            skLineSegment(sketch, "E221", {"start": v(-20.4, 5.18) * mm, "end": v(-17.23, 5.18) * mm});
            skFitSpline(sketch, "E222", {"points": [v(-13.82, 4.3) * mm, v(-14.7, 4.98) * mm, v(-15.07, 6.4) * mm, v(-14.67, 7.61) * mm]});
            skFitSpline(sketch, "E223", {"points": [v(-14.67, 7.61) * mm, v(-13.73, 10.47) * mm, v(-9.92, 9.64) * mm, v(-9.92, 6.57) * mm]});
            skFitSpline(sketch, "E224", {"points": [v(-9.92, 6.57) * mm, v(-9.92, 4.44) * mm, v(-12.23, 3.1) * mm, v(-13.82, 4.3) * mm]});
            skFitSpline(sketch, "E225", {"points": [v(-11.2, 4.86) * mm, v(-9.9, 6.16) * mm, v(-10.76, 9) * mm, v(-12.44, 9) * mm]});
            skFitSpline(sketch, "E226", {"points": [v(-12.44, 9) * mm, v(-13.2, 9) * mm, v(-14.37, 7.56) * mm, v(-14.37, 6.61) * mm]});
            skFitSpline(sketch, "E227", {"points": [v(-14.37, 6.61) * mm, v(-14.37, 5.67) * mm, v(-13.2, 4.23) * mm, v(-12.44, 4.23) * mm]});
            skFitSpline(sketch, "E228", {"points": [v(-12.44, 4.23) * mm, v(-12.1, 4.23) * mm, v(-11.54, 4.51) * mm, v(-11.2, 4.86) * mm]});
            skFitSpline(sketch, "E229", {"points": [v(-5.03, 4.37) * mm, v(-7.08, 5.26) * mm, v(-6.95, 8.21) * mm, v(-4.82, 8.95) * mm]});
            skFitSpline(sketch, "E230", {"points": [v(-4.82, 8.95) * mm, v(-3.55, 9.4) * mm, v(-2.93, 9.41) * mm, v(-2.93, 9) * mm]});
            skFitSpline(sketch, "E231", {"points": [v(-2.93, 9) * mm, v(-2.93, 8.82) * mm, v(-3.3, 8.68) * mm, v(-3.74, 8.68) * mm]});
            skFitSpline(sketch, "E232", {"points": [v(-3.74, 8.68) * mm, v(-4.88, 8.68) * mm, v(-6.2, 7.28) * mm, v(-5.94, 6.37) * mm]});
            skFitSpline(sketch, "E233", {"points": [v(-5.94, 6.37) * mm, v(-5.68, 5.47) * mm, v(-4.63, 4.55) * mm, v(-3.87, 4.55) * mm]});
            skFitSpline(sketch, "E234", {"points": [v(-3.87, 4.55) * mm, v(-3.55, 4.55) * mm, v(-3.2, 4.4) * mm, v(-3.1, 4.23) * mm]});
            skFitSpline(sketch, "E235", {"points": [v(-3.1, 4.23) * mm, v(-2.81, 3.78) * mm, v(-3.86, 3.86) * mm, v(-5.03, 4.37) * mm]});
            skFitSpline(sketch, "E236", {"points": [v(-1.23, 6.61) * mm, v(-1.23, 8.18) * mm, v(-1.18, 8.94) * mm, v(-1.11, 8.28) * mm]});
            skFitSpline(sketch, "E237", {"points": [v(2.47, 8.2) * mm, v(2.47, 8.81) * mm, v(2.61, 9.31) * mm, v(2.79, 9.31) * mm]});
            skFitSpline(sketch, "E238", {"points": [v(2.79, 9.31) * mm, v(2.98, 9.31) * mm, v(3.1, 8.2) * mm, v(3.1, 6.61) * mm]});
            skFitSpline(sketch, "E239", {"points": [v(3.1, 6.61) * mm, v(3.1, 5.02) * mm, v(2.98, 3.91) * mm, v(2.79, 3.91) * mm]});
            skFitSpline(sketch, "E240", {"points": [v(2.79, 3.91) * mm, v(2.61, 3.91) * mm, v(2.47, 4.48) * mm, v(2.47, 5.18) * mm]});
            skLineSegment(sketch, "E241", {"start": v(-1.11, 8.28) * mm, "end": v(-0.99, 7.09) * mm});
            skLineSegment(sketch, "E242", {"start": v(-0.99, 7.09) * mm, "end": v(0.74, 7.09) * mm});
            skLineSegment(sketch, "E243", {"start": v(0.74, 7.09) * mm, "end": v(2.47, 7.09) * mm});
            skLineSegment(sketch, "E244", {"start": v(2.47, 7.09) * mm, "end": v(2.47, 8.2) * mm});
            skLineSegment(sketch, "E245", {"start": v(2.47, 8.2) * mm, "end": v(-1.11, 8.28) * mm});
            skFitSpline(sketch, "E246", {"points": [v(-1.1, 5.1) * mm, v(-1.18, 4.36) * mm, v(-1.23, 5.04) * mm, v(-1.23, 6.61) * mm]});
            skLineSegment(sketch, "E247", {"start": v(2.47, 5.18) * mm, "end": v(2.47, 6.45) * mm});
            skLineSegment(sketch, "E248", {"start": v(2.47, 6.45) * mm, "end": v(0.74, 6.45) * mm});
            skLineSegment(sketch, "E249", {"start": v(0.74, 6.45) * mm, "end": v(-0.99, 6.45) * mm});
            skLineSegment(sketch, "E250", {"start": v(-0.99, 6.45) * mm, "end": v(-1.1, 5.1) * mm});
            skLineSegment(sketch, "E251", {"start": v(-1.1, 5.1) * mm, "end": v(2.47, 5.18) * mm});
            skFitSpline(sketch, "E252", {"points": [v(4.38, 4.21) * mm, v(4.38, 4.77) * mm, v(6.56, 9.31) * mm, v(6.83, 9.31) * mm]});
            skFitSpline(sketch, "E253", {"points": [v(6.83, 9.31) * mm, v(7.25, 9.31) * mm, v(9.44, 4.25) * mm, v(9.1, 4.05) * mm]});
            skFitSpline(sketch, "E254", {"points": [v(9.1, 4.05) * mm, v(8.94, 3.95) * mm, v(8.66, 4.3) * mm, v(8.47, 4.84) * mm]});
            skFitSpline(sketch, "E255", {"points": [v(8.47, 4.84) * mm, v(8.16, 5.73) * mm, v(8, 5.82) * mm, v(6.76, 5.82) * mm]});
            skFitSpline(sketch, "E256", {"points": [v(6.76, 5.82) * mm, v(5.53, 5.82) * mm, v(5.36, 5.72) * mm, v(5.06, 4.86) * mm]});
            skFitSpline(sketch, "E257", {"points": [v(5.06, 4.86) * mm, v(4.74, 3.94) * mm, v(4.38, 3.6) * mm, v(4.38, 4.21) * mm]});
            skFitSpline(sketch, "E258", {"points": [v(7.56, 6.8) * mm, v(7.56, 6.98) * mm, v(7.4, 7.43) * mm, v(7.2, 7.8) * mm]});
            skFitSpline(sketch, "E259", {"points": [v(7.2, 7.8) * mm, v(6.84, 8.47) * mm, v(6.84, 8.47) * mm, v(6.41, 7.7) * mm]});
            skFitSpline(sketch, "E260", {"points": [v(6.41, 7.7) * mm, v(5.81, 6.62) * mm, v(5.86, 6.45) * mm, v(6.76, 6.45) * mm]});
            skFitSpline(sketch, "E261", {"points": [v(6.76, 6.45) * mm, v(7.2, 6.45) * mm, v(7.56, 6.6) * mm, v(7.56, 6.8) * mm]});
            skFitSpline(sketch, "E262", {"points": [v(10.42, 6.43) * mm, v(10.42, 7.82) * mm, v(10.55, 9.04) * mm, v(10.7, 9.14) * mm]});
            skFitSpline(sketch, "E263", {"points": [v(10.7, 9.14) * mm, v(10.86, 9.23) * mm, v(11.76, 8.35) * mm, v(12.7, 7.18) * mm]});
            skFitSpline(sketch, "E264", {"points": [v(14.14, 4.57) * mm, v(13.75, 5.01) * mm, v(12.9, 6.01) * mm, v(12.26, 6.79) * mm]});
            skLineSegment(sketch, "E265", {"start": v(12.7, 7.18) * mm, "end": v(14.39, 5.04) * mm});
            skLineSegment(sketch, "E266", {"start": v(14.39, 5.04) * mm, "end": v(14.57, 7.26) * mm});
            skLineSegment(sketch, "E267", {"start": v(14.57, 7.26) * mm, "end": v(14.75, 9.47) * mm});
            skLineSegment(sketch, "E268", {"start": v(14.75, 9.47) * mm, "end": v(14.8, 6.61) * mm});
            skLineSegment(sketch, "E269", {"start": v(14.8, 6.61) * mm, "end": v(14.84, 3.75) * mm});
            skLineSegment(sketch, "E270", {"start": v(14.84, 3.75) * mm, "end": v(14.14, 4.57) * mm});
            skLineSegment(sketch, "E271", {"start": v(14.14, 4.57) * mm, "end": v(12.7, 7.18) * mm});
            skFitSpline(sketch, "E272", {"points": [v(11.06, 6.06) * mm, v(11.06, 4.85) * mm, v(10.91, 3.91) * mm, v(10.73, 3.91) * mm]});
            skFitSpline(sketch, "E273", {"points": [v(10.73, 3.91) * mm, v(10.55, 3.91) * mm, v(10.42, 4.96) * mm, v(10.42, 6.43) * mm]});
            skLineSegment(sketch, "E274", {"start": v(12.26, 6.79) * mm, "end": v(11.08, 8.2) * mm});
            skLineSegment(sketch, "E275", {"start": v(11.08, 8.2) * mm, "end": v(11.06, 6.06) * mm});
            skLineSegment(sketch, "E276", {"start": v(11.06, 6.06) * mm, "end": v(12.26, 6.79) * mm});
            skFitSpline(sketch, "E277", {"points": [v(18.16, 4.37) * mm, v(16.12, 5.26) * mm, v(16.25, 8.21) * mm, v(18.37, 8.95) * mm]});
            skFitSpline(sketch, "E278", {"points": [v(18.37, 8.95) * mm, v(19.65, 9.4) * mm, v(20.58, 9.42) * mm, v(20.58, 9) * mm]});
            skFitSpline(sketch, "E279", {"points": [v(20.58, 9) * mm, v(20.58, 8.82) * mm, v(20.15, 8.68) * mm, v(19.62, 8.68) * mm]});
            skFitSpline(sketch, "E280", {"points": [v(19.62, 8.68) * mm, v(18.59, 8.68) * mm, v(17.09, 7.48) * mm, v(17.09, 6.66) * mm]});
            skFitSpline(sketch, "E281", {"points": [v(17.09, 6.66) * mm, v(17.09, 5.9) * mm, v(18.14, 4.87) * mm, v(19.23, 4.56) * mm]});
            skLineSegment(sketch, "E282", {"start": v(10.42, 6.43) * mm, "end": v(10.42, 6.43) * mm});
            skFitSpline(sketch, "E283", {"points": [v(20.27, 5.52) * mm, v(20.27, 6.2) * mm, v(20.4, 6.77) * mm, v(20.58, 6.77) * mm]});
            skFitSpline(sketch, "E284", {"points": [v(20.58, 6.77) * mm, v(20.76, 6.77) * mm, v(20.9, 6.13) * mm, v(20.9, 5.34) * mm]});
            skFitSpline(sketch, "E285", {"points": [v(20.9, 5.34) * mm, v(20.9, 3.99) * mm, v(20.85, 3.91) * mm, v(20.03, 3.92) * mm]});
            skFitSpline(sketch, "E286", {"points": [v(20.03, 3.92) * mm, v(19.55, 3.93) * mm, v(18.7, 4.13) * mm, v(18.16, 4.37) * mm]});
            skLineSegment(sketch, "E287", {"start": v(19.23, 4.56) * mm, "end": v(20.27, 4.27) * mm});
            skLineSegment(sketch, "E288", {"start": v(20.27, 4.27) * mm, "end": v(20.27, 5.52) * mm});
            skLineSegment(sketch, "E289", {"start": v(20.27, 5.52) * mm, "end": v(19.23, 4.56) * mm});
            skFitSpline(sketch, "E290", {"points": [v(24.4, 9.31) * mm, v(25.27, 9.31) * mm, v(25.99, 9.17) * mm, v(25.99, 9) * mm]});
            skFitSpline(sketch, "E291", {"points": [v(25.99, 9) * mm, v(25.99, 8.82) * mm, v(25.34, 8.68) * mm, v(24.56, 8.68) * mm]});
            skFitSpline(sketch, "E292", {"points": [v(24.56, 8.68) * mm, v(23.24, 8.68) * mm, v(23.13, 8.61) * mm, v(23.13, 7.88) * mm]});
            skFitSpline(sketch, "E293", {"points": [v(23.13, 7.88) * mm, v(23.13, 7.15) * mm, v(23.24, 7.09) * mm, v(24.56, 7.09) * mm]});
            skFitSpline(sketch, "E294", {"points": [v(24.56, 7.09) * mm, v(25.34, 7.09) * mm, v(25.99, 6.95) * mm, v(25.99, 6.77) * mm]});
            skFitSpline(sketch, "E295", {"points": [v(25.99, 6.77) * mm, v(25.99, 6.6) * mm, v(25.34, 6.45) * mm, v(24.56, 6.45) * mm]});
            skFitSpline(sketch, "E296", {"points": [v(24.56, 6.45) * mm, v(23.18, 6.45) * mm, v(23.13, 6.42) * mm, v(23.13, 5.5) * mm]});
            skFitSpline(sketch, "E297", {"points": [v(23.13, 5.5) * mm, v(23.13, 4.58) * mm, v(23.18, 4.55) * mm, v(24.56, 4.55) * mm]});
            skFitSpline(sketch, "E298", {"points": [v(24.56, 4.55) * mm, v(25.34, 4.55) * mm, v(25.99, 4.4) * mm, v(25.99, 4.23) * mm]});
            skFitSpline(sketch, "E299", {"points": [v(25.99, 4.23) * mm, v(25.99, 4.05) * mm, v(25.27, 3.91) * mm, v(24.4, 3.91) * mm]});
            skLineSegment(sketch, "E300", {"start": v(22.8, 6.61) * mm, "end": v(22.8, 9.31) * mm});
            skLineSegment(sketch, "E301", {"start": v(22.8, 9.31) * mm, "end": v(24.4, 9.31) * mm});
            skLineSegment(sketch, "E302", {"start": v(24.4, 9.31) * mm, "end": v(22.8, 6.61) * mm});
            skFitSpline(sketch, "E303", {"points": [v(28.21, 4.36) * mm, v(29.7, 4.9) * mm, v(29.74, 5.54) * mm, v(28.38, 6.58) * mm]});
            skFitSpline(sketch, "E304", {"points": [v(28.38, 6.58) * mm, v(27.15, 7.52) * mm, v(27, 8.06) * mm, v(27.76, 8.81) * mm]});
            skFitSpline(sketch, "E305", {"points": [v(27.76, 8.81) * mm, v(28.32, 9.38) * mm, v(30.12, 9.5) * mm, v(30.12, 8.96) * mm]});
            skFitSpline(sketch, "E306", {"points": [v(30.12, 8.96) * mm, v(30.12, 8.77) * mm, v(29.94, 8.68) * mm, v(29.72, 8.76) * mm]});
            skFitSpline(sketch, "E307", {"points": [v(29.72, 8.76) * mm, v(29.14, 8.98) * mm, v(27.9, 8.44) * mm, v(27.9, 7.97) * mm]});
            skFitSpline(sketch, "E308", {"points": [v(27.9, 7.97) * mm, v(27.9, 7.75) * mm, v(28.4, 7.24) * mm, v(29, 6.85) * mm]});
            skFitSpline(sketch, "E309", {"points": [v(29, 6.85) * mm, v(30.9, 5.62) * mm, v(30.29, 3.87) * mm, v(28, 3.94) * mm]});
            skFitSpline(sketch, "E310", {"points": [v(28, 3.94) * mm, v(27.12, 3.96) * mm, v(27.12, 3.97) * mm, v(28.21, 4.36) * mm]});
            skLineSegment(sketch, "E311", {"start": v(24.4, 3.91) * mm, "end": v(22.8, 3.91) * mm});
            skLineSegment(sketch, "E312", {"start": v(22.8, 3.91) * mm, "end": v(22.8, 6.61) * mm});
            skLineSegment(sketch, "E313", {"start": v(22.8, 6.61) * mm, "end": v(24.4, 3.91) * mm});
            skFitSpline(sketch, "E314", {"points": [v(-40.07, 19.36) * mm, v(-40.1, 20.29) * mm, v(-40.38, 21.01) * mm, v(-41.06, 21.86) * mm]});
            skFitSpline(sketch, "E315", {"points": [v(-41.06, 21.86) * mm, v(-42.36, 23.5) * mm, v(-42.26, 24.08) * mm, v(-40.95, 22.55) * mm]});
            skFitSpline(sketch, "E316", {"points": [v(-38.9, 22.55) * mm, v(-38.36, 23.22) * mm, v(-37.9, 23.6) * mm, v(-37.9, 23.4) * mm]});
            skFitSpline(sketch, "E317", {"points": [v(-37.9, 23.4) * mm, v(-37.9, 23.2) * mm, v(-38.28, 22.56) * mm, v(-38.75, 22) * mm]});
            skFitSpline(sketch, "E318", {"points": [v(-38.75, 22) * mm, v(-39.28, 21.36) * mm, v(-39.7, 20.41) * mm, v(-39.82, 19.51) * mm]});
            skLineSegment(sketch, "E319", {"start": v(-40.95, 22.55) * mm, "end": v(-39.9, 21.33) * mm});
            skLineSegment(sketch, "E320", {"start": v(-39.9, 21.33) * mm, "end": v(-38.9, 22.55) * mm});
            skLineSegment(sketch, "E321", {"start": v(-38.9, 22.55) * mm, "end": v(-40.95, 22.55) * mm});
            skFitSpline(sketch, "E322", {"points": [v(-36.27, 19.05) * mm, v(-37.69, 20.85) * mm, v(-36.63, 23.61) * mm, v(-34.53, 23.61) * mm]});
            skFitSpline(sketch, "E323", {"points": [v(-34.53, 23.61) * mm, v(-32.6, 23.61) * mm, v(-31.4, 21.66) * mm, v(-32.17, 19.78) * mm]});
            skFitSpline(sketch, "E324", {"points": [v(-32.17, 19.78) * mm, v(-32.91, 18) * mm, v(-35.14, 17.6) * mm, v(-36.27, 19.05) * mm]});
            skLineSegment(sketch, "E325", {"start": v(-39.82, 19.51) * mm, "end": v(-40.03, 18.05) * mm});
            skLineSegment(sketch, "E326", {"start": v(-40.03, 18.05) * mm, "end": v(-40.07, 19.36) * mm});
            skLineSegment(sketch, "E327", {"start": v(-40.07, 19.36) * mm, "end": v(-39.82, 19.51) * mm});
            skFitSpline(sketch, "E328", {"points": [v(-33.14, 19.37) * mm, v(-32.78, 19.83) * mm, v(-32.48, 20.52) * mm, v(-32.48, 20.91) * mm]});
            skFitSpline(sketch, "E329", {"points": [v(-32.48, 20.91) * mm, v(-32.48, 21.86) * mm, v(-33.65, 23.3) * mm, v(-34.41, 23.3) * mm]});
            skFitSpline(sketch, "E330", {"points": [v(-34.41, 23.3) * mm, v(-35.4, 23.3) * mm, v(-36.3, 22.15) * mm, v(-36.3, 20.91) * mm]});
            skFitSpline(sketch, "E331", {"points": [v(-36.3, 20.91) * mm, v(-36.3, 19.67) * mm, v(-35.4, 18.53) * mm, v(-34.41, 18.53) * mm]});
            skFitSpline(sketch, "E332", {"points": [v(-34.41, 18.53) * mm, v(-34.08, 18.53) * mm, v(-33.5, 18.9) * mm, v(-33.14, 19.37) * mm]});
            skFitSpline(sketch, "E333", {"points": [v(-29.76, 18.7) * mm, v(-30.03, 18.98) * mm, v(-30.26, 19.66) * mm, v(-30.26, 20.22) * mm]});
            skFitSpline(sketch, "E334", {"points": [v(-30.26, 20.22) * mm, v(-30.26, 20.77) * mm, v(-30.36, 21.77) * mm, v(-30.46, 22.42) * mm]});
            skFitSpline(sketch, "E335", {"points": [v(-30.46, 22.42) * mm, v(-30.6, 23.21) * mm, v(-30.54, 23.61) * mm, v(-30.3, 23.61) * mm]});
            skFitSpline(sketch, "E336", {"points": [v(-30.3, 23.61) * mm, v(-30.07, 23.61) * mm, v(-29.94, 22.91) * mm, v(-29.94, 21.7) * mm]});
            skFitSpline(sketch, "E337", {"points": [v(-29.94, 21.7) * mm, v(-29.94, 20.22) * mm, v(-29.8, 19.66) * mm, v(-29.3, 19.16) * mm]});
            skFitSpline(sketch, "E338", {"points": [v(-29.3, 19.16) * mm, v(-28.59, 18.44) * mm, v(-28.25, 18.39) * mm, v(-27.38, 18.86) * mm]});
            skFitSpline(sketch, "E339", {"points": [v(-27.38, 18.86) * mm, v(-26.86, 19.13) * mm, v(-26.76, 19.54) * mm, v(-26.76, 21.4) * mm]});
            skFitSpline(sketch, "E340", {"points": [v(-26.76, 21.4) * mm, v(-26.76, 22.66) * mm, v(-26.63, 23.61) * mm, v(-26.45, 23.61) * mm]});
            skFitSpline(sketch, "E341", {"points": [v(-26.45, 23.61) * mm, v(-26.27, 23.61) * mm, v(-26.13, 22.68) * mm, v(-26.13, 21.44) * mm]});
            skFitSpline(sketch, "E342", {"points": [v(-26.13, 21.44) * mm, v(-26.13, 19.73) * mm, v(-26.25, 19.15) * mm, v(-26.7, 18.74) * mm]});
            skFitSpline(sketch, "E343", {"points": [v(-26.7, 18.74) * mm, v(-27.44, 18.07) * mm, v(-29.1, 18.06) * mm, v(-29.76, 18.7) * mm]});
            skFitSpline(sketch, "E344", {"points": [v(-22.3, 18.85) * mm, v(-22.3, 19.28) * mm, v(-22.18, 20.14) * mm, v(-22.03, 20.75) * mm]});
            skFitSpline(sketch, "E345", {"points": [v(-22.03, 20.75) * mm, v(-21.87, 21.36) * mm, v(-21.65, 22.26) * mm, v(-21.55, 22.74) * mm]});
            skFitSpline(sketch, "E346", {"points": [v(-21.55, 22.74) * mm, v(-21.44, 23.22) * mm, v(-21.23, 23.61) * mm, v(-21.08, 23.61) * mm]});
            skFitSpline(sketch, "E347", {"points": [v(-21.08, 23.61) * mm, v(-20.93, 23.61) * mm, v(-20.43, 22.75) * mm, v(-19.96, 21.7) * mm]});
            skFitSpline(sketch, "E348", {"points": [v(-19.96, 21.7) * mm, v(-19.49, 20.66) * mm, v(-19.03, 19.8) * mm, v(-18.95, 19.8) * mm]});
            skFitSpline(sketch, "E349", {"points": [v(-18.95, 19.8) * mm, v(-18.87, 19.8) * mm, v(-18.43, 20.66) * mm, v(-17.97, 21.7) * mm]});
            skFitSpline(sketch, "E350", {"points": [v(-17.97, 21.7) * mm, v(-17.1, 23.74) * mm, v(-16.7, 24.05) * mm, v(-16.46, 22.9) * mm]});
            skFitSpline(sketch, "E351", {"points": [v(-16.46, 22.9) * mm, v(-15.58, 18.73) * mm, v(-15.52, 18.21) * mm, v(-15.92, 18.21) * mm]});
            skFitSpline(sketch, "E352", {"points": [v(-15.92, 18.21) * mm, v(-16.08, 18.21) * mm, v(-16.3, 18.89) * mm, v(-16.42, 19.72) * mm]});
            skFitSpline(sketch, "E353", {"points": [v(-16.42, 19.72) * mm, v(-16.88, 22.92) * mm, v(-16.92, 22.95) * mm, v(-17.9, 20.8) * mm]});
            skFitSpline(sketch, "E354", {"points": [v(-17.9, 20.8) * mm, v(-18.38, 19.73) * mm, v(-18.9, 18.85) * mm, v(-19.06, 18.85) * mm]});
            skFitSpline(sketch, "E355", {"points": [v(-19.06, 18.85) * mm, v(-19.21, 18.85) * mm, v(-19.66, 19.63) * mm, v(-20.06, 20.6) * mm]});
            skFitSpline(sketch, "E356", {"points": [v(-20.06, 20.6) * mm, v(-20.46, 21.56) * mm, v(-20.9, 22.27) * mm, v(-21.06, 22.18) * mm]});
            skFitSpline(sketch, "E357", {"points": [v(-21.06, 22.18) * mm, v(-21.2, 22.08) * mm, v(-21.42, 21.33) * mm, v(-21.54, 20.5) * mm]});
            skFitSpline(sketch, "E358", {"points": [v(-21.54, 20.5) * mm, v(-21.8, 18.7) * mm, v(-22.3, 17.63) * mm, v(-22.3, 18.85) * mm]});
            skFitSpline(sketch, "E359", {"points": [v(-12.46, 23.61) * mm, v(-11.6, 23.61) * mm, v(-10.88, 23.47) * mm, v(-10.88, 23.3) * mm]});
            skFitSpline(sketch, "E360", {"points": [v(-10.88, 23.3) * mm, v(-10.88, 23.12) * mm, v(-11.52, 22.98) * mm, v(-12.3, 22.98) * mm]});
            skFitSpline(sketch, "E361", {"points": [v(-12.3, 22.98) * mm, v(-13.62, 22.98) * mm, v(-13.74, 22.91) * mm, v(-13.74, 22.18) * mm]});
            skFitSpline(sketch, "E362", {"points": [v(-13.74, 22.18) * mm, v(-13.74, 21.45) * mm, v(-13.62, 21.39) * mm, v(-12.3, 21.39) * mm]});
            skFitSpline(sketch, "E363", {"points": [v(-12.3, 21.39) * mm, v(-11.52, 21.39) * mm, v(-10.88, 21.25) * mm, v(-10.88, 21.07) * mm]});
            skFitSpline(sketch, "E364", {"points": [v(-10.88, 21.07) * mm, v(-10.88, 20.9) * mm, v(-11.52, 20.75) * mm, v(-12.3, 20.75) * mm]});
            skFitSpline(sketch, "E365", {"points": [v(-12.3, 20.75) * mm, v(-13.68, 20.75) * mm, v(-13.74, 20.72) * mm, v(-13.74, 19.8) * mm]});
            skFitSpline(sketch, "E366", {"points": [v(-13.74, 19.8) * mm, v(-13.74, 18.88) * mm, v(-13.68, 18.85) * mm, v(-12.3, 18.85) * mm]});
            skFitSpline(sketch, "E367", {"points": [v(-12.3, 18.85) * mm, v(-11.52, 18.85) * mm, v(-10.88, 18.7) * mm, v(-10.88, 18.53) * mm]});
            skFitSpline(sketch, "E368", {"points": [v(-10.88, 18.53) * mm, v(-10.88, 18.35) * mm, v(-11.6, 18.21) * mm, v(-12.46, 18.21) * mm]});
            skLineSegment(sketch, "E369", {"start": v(-14.05, 20.91) * mm, "end": v(-14.05, 23.61) * mm});
            skLineSegment(sketch, "E370", {"start": v(-14.05, 23.61) * mm, "end": v(-12.46, 23.61) * mm});
            skLineSegment(sketch, "E371", {"start": v(-12.46, 23.61) * mm, "end": v(-14.05, 20.91) * mm});
            skLineSegment(sketch, "E372", {"start": v(-12.46, 18.21) * mm, "end": v(-14.05, 18.21) * mm});
            skLineSegment(sketch, "E373", {"start": v(-14.05, 18.21) * mm, "end": v(-14.05, 20.91) * mm});
            skLineSegment(sketch, "E374", {"start": v(-14.05, 20.91) * mm, "end": v(-12.46, 18.21) * mm});
            skFitSpline(sketch, "E375", {"points": [v(-7.7, 23.61) * mm, v(-6.82, 23.61) * mm, v(-6.1, 23.47) * mm, v(-6.1, 23.3) * mm]});
            skFitSpline(sketch, "E376", {"points": [v(-6.1, 23.3) * mm, v(-6.1, 23.12) * mm, v(-6.68, 22.98) * mm, v(-7.38, 22.98) * mm]});
            skFitSpline(sketch, "E377", {"points": [v(-7.38, 22.98) * mm, v(-8.52, 22.98) * mm, v(-8.65, 22.9) * mm, v(-8.65, 22.18) * mm]});
            skFitSpline(sketch, "E378", {"points": [v(-8.65, 22.18) * mm, v(-8.65, 21.47) * mm, v(-8.52, 21.39) * mm, v(-7.38, 21.39) * mm]});
            skFitSpline(sketch, "E379", {"points": [v(-7.38, 21.39) * mm, v(-6.68, 21.39) * mm, v(-6.1, 21.25) * mm, v(-6.1, 21.07) * mm]});
            skFitSpline(sketch, "E380", {"points": [v(-6.1, 21.07) * mm, v(-6.1, 20.9) * mm, v(-6.68, 20.75) * mm, v(-7.38, 20.75) * mm]});
            skFitSpline(sketch, "E381", {"points": [v(-7.38, 20.75) * mm, v(-8.58, 20.75) * mm, v(-8.65, 20.7) * mm, v(-8.65, 19.8) * mm]});
            skFitSpline(sketch, "E382", {"points": [v(-8.65, 19.8) * mm, v(-8.65, 18.9) * mm, v(-8.58, 18.85) * mm, v(-7.4, 18.85) * mm]});
            skFitSpline(sketch, "E383", {"points": [v(-7.4, 18.85) * mm, v(-6.7, 18.85) * mm, v(-6.06, 18.7) * mm, v(-5.95, 18.53) * mm]});
            skFitSpline(sketch, "E384", {"points": [v(-5.95, 18.53) * mm, v(-5.83, 18.33) * mm, v(-6.42, 18.21) * mm, v(-7.52, 18.21) * mm]});
            skLineSegment(sketch, "E385", {"start": v(-9.29, 20.91) * mm, "end": v(-9.29, 23.61) * mm});
            skLineSegment(sketch, "E386", {"start": v(-9.29, 23.61) * mm, "end": v(-7.7, 23.61) * mm});
            skLineSegment(sketch, "E387", {"start": v(-7.7, 23.61) * mm, "end": v(-9.29, 20.91) * mm});
            skLineSegment(sketch, "E388", {"start": v(-7.52, 18.21) * mm, "end": v(-9.29, 18.21) * mm});
            skLineSegment(sketch, "E389", {"start": v(-9.29, 18.21) * mm, "end": v(-9.29, 20.91) * mm});
            skLineSegment(sketch, "E390", {"start": v(-9.29, 20.91) * mm, "end": v(-7.52, 18.21) * mm});
            skFitSpline(sketch, "E391", {"points": [v(-4.04, 22.98) * mm, v(-4.66, 22.98) * mm, v(-5.16, 23.12) * mm, v(-5.16, 23.3) * mm]});
            skFitSpline(sketch, "E392", {"points": [v(-5.16, 23.3) * mm, v(-5.16, 23.48) * mm, v(-4.14, 23.61) * mm, v(-2.75, 23.61) * mm]});
            skFitSpline(sketch, "E393", {"points": [v(-2.75, 23.61) * mm, v(-1.23, 23.61) * mm, v(-0.42, 23.5) * mm, v(-0.55, 23.3) * mm]});
            skFitSpline(sketch, "E394", {"points": [v(-0.55, 23.3) * mm, v(-0.66, 23.12) * mm, v(-1.16, 22.98) * mm, v(-1.67, 22.98) * mm]});
            skLineSegment(sketch, "E395", {"start": v(-2.87, 20.51) * mm, "end": v(-2.93, 22.98) * mm});
            skLineSegment(sketch, "E396", {"start": v(-2.93, 22.98) * mm, "end": v(-4.04, 22.98) * mm});
            skLineSegment(sketch, "E397", {"start": v(-4.04, 22.98) * mm, "end": v(-2.87, 20.51) * mm});
            skFitSpline(sketch, "E398", {"points": [v(3.1, 18.66) * mm, v(4.59, 19.2) * mm, v(4.64, 19.84) * mm, v(3.28, 20.88) * mm]});
            skFitSpline(sketch, "E399", {"points": [v(3.28, 20.88) * mm, v(2.04, 21.82) * mm, v(1.9, 22.35) * mm, v(2.65, 23.11) * mm]});
            skFitSpline(sketch, "E400", {"points": [v(2.65, 23.11) * mm, v(3.22, 23.68) * mm, v(5.01, 23.8) * mm, v(5.01, 23.26) * mm]});
            skFitSpline(sketch, "E401", {"points": [v(5.01, 23.26) * mm, v(5.01, 23.07) * mm, v(4.83, 22.98) * mm, v(4.62, 23.06) * mm]});
            skFitSpline(sketch, "E402", {"points": [v(4.62, 23.06) * mm, v(4.03, 23.28) * mm, v(2.79, 22.74) * mm, v(2.8, 22.27) * mm]});
            skFitSpline(sketch, "E403", {"points": [v(2.8, 22.27) * mm, v(2.8, 22.05) * mm, v(3.3, 21.54) * mm, v(3.9, 21.15) * mm]});
            skFitSpline(sketch, "E404", {"points": [v(3.9, 21.15) * mm, v(5.8, 19.92) * mm, v(5.18, 18.17) * mm, v(2.89, 18.23) * mm]});
            skFitSpline(sketch, "E405", {"points": [v(2.89, 18.23) * mm, v(2.01, 18.26) * mm, v(2.02, 18.27) * mm, v(3.1, 18.66) * mm]});
            skLineSegment(sketch, "E406", {"start": v(-1.67, 22.98) * mm, "end": v(-2.59, 22.98) * mm});
            skLineSegment(sketch, "E407", {"start": v(-2.59, 22.98) * mm, "end": v(-2.7, 20.51) * mm});
            skLineSegment(sketch, "E408", {"start": v(-2.7, 20.51) * mm, "end": v(-2.8, 18.05) * mm});
            skLineSegment(sketch, "E409", {"start": v(-2.8, 18.05) * mm, "end": v(-2.87, 20.51) * mm});
            skLineSegment(sketch, "E410", {"start": v(-2.87, 20.51) * mm, "end": v(-1.67, 22.98) * mm});
            skFitSpline(sketch, "E411", {"points": [v(7.47, 18.6) * mm, v(6.59, 19.28) * mm, v(6.22, 20.7) * mm, v(6.62, 21.91) * mm]});
            skFitSpline(sketch, "E412", {"points": [v(6.62, 21.91) * mm, v(7.56, 24.77) * mm, v(11.37, 23.94) * mm, v(11.37, 20.87) * mm]});
            skFitSpline(sketch, "E413", {"points": [v(11.37, 20.87) * mm, v(11.37, 18.73) * mm, v(9.06, 17.4) * mm, v(7.47, 18.6) * mm]});
            skFitSpline(sketch, "E414", {"points": [v(10.1, 19.16) * mm, v(11.4, 20.46) * mm, v(10.53, 23.3) * mm, v(8.85, 23.3) * mm]});
            skFitSpline(sketch, "E415", {"points": [v(8.85, 23.3) * mm, v(8.08, 23.3) * mm, v(6.92, 21.86) * mm, v(6.92, 20.91) * mm]});
            skFitSpline(sketch, "E416", {"points": [v(6.92, 20.91) * mm, v(6.92, 19.97) * mm, v(8.08, 18.53) * mm, v(8.85, 18.53) * mm]});
            skFitSpline(sketch, "E417", {"points": [v(8.85, 18.53) * mm, v(9.19, 18.53) * mm, v(9.75, 18.81) * mm, v(10.1, 19.16) * mm]});
            skFitSpline(sketch, "E418", {"points": [v(12.65, 18.85) * mm, v(12.65, 19.28) * mm, v(12.77, 20.14) * mm, v(12.93, 20.75) * mm]});
            skFitSpline(sketch, "E419", {"points": [v(12.93, 20.75) * mm, v(13.09, 21.36) * mm, v(13.3, 22.26) * mm, v(13.4, 22.74) * mm]});
            skFitSpline(sketch, "E420", {"points": [v(13.4, 22.74) * mm, v(13.52, 23.22) * mm, v(13.73, 23.61) * mm, v(13.87, 23.61) * mm]});
            skFitSpline(sketch, "E421", {"points": [v(13.87, 23.61) * mm, v(14.02, 23.61) * mm, v(14.53, 22.75) * mm, v(15, 21.7) * mm]});
            skFitSpline(sketch, "E422", {"points": [v(15, 21.7) * mm, v(15.47, 20.66) * mm, v(15.92, 19.8) * mm, v(16, 19.8) * mm]});
            skFitSpline(sketch, "E423", {"points": [v(16, 19.8) * mm, v(16.09, 19.8) * mm, v(16.53, 20.66) * mm, v(16.98, 21.7) * mm]});
            skFitSpline(sketch, "E424", {"points": [v(16.98, 21.7) * mm, v(17.86, 23.74) * mm, v(18.26, 24.05) * mm, v(18.5, 22.9) * mm]});
            skFitSpline(sketch, "E425", {"points": [v(18.5, 22.9) * mm, v(19.37, 18.73) * mm, v(19.43, 18.21) * mm, v(19.03, 18.21) * mm]});
            skFitSpline(sketch, "E426", {"points": [v(19.03, 18.21) * mm, v(18.88, 18.21) * mm, v(18.65, 18.89) * mm, v(18.53, 19.72) * mm]});
            skFitSpline(sketch, "E427", {"points": [v(18.53, 19.72) * mm, v(18.07, 22.92) * mm, v(18.03, 22.95) * mm, v(17.06, 20.8) * mm]});
            skFitSpline(sketch, "E428", {"points": [v(17.06, 20.8) * mm, v(16.57, 19.73) * mm, v(16.05, 18.85) * mm, v(15.9, 18.85) * mm]});
            skFitSpline(sketch, "E429", {"points": [v(15.9, 18.85) * mm, v(15.74, 18.85) * mm, v(15.3, 19.63) * mm, v(14.9, 20.6) * mm]});
            skFitSpline(sketch, "E430", {"points": [v(14.9, 20.6) * mm, v(14.5, 21.56) * mm, v(14.05, 22.27) * mm, v(13.9, 22.18) * mm]});
            skFitSpline(sketch, "E431", {"points": [v(13.9, 22.18) * mm, v(13.75, 22.08) * mm, v(13.53, 21.33) * mm, v(13.41, 20.5) * mm]});
            skFitSpline(sketch, "E432", {"points": [v(13.41, 20.5) * mm, v(13.15, 18.7) * mm, v(12.66, 17.63) * mm, v(12.65, 18.85) * mm]});
            skFitSpline(sketch, "E433", {"points": [v(22.5, 23.61) * mm, v(23.36, 23.61) * mm, v(24.08, 23.47) * mm, v(24.08, 23.3) * mm]});
            skFitSpline(sketch, "E434", {"points": [v(24.08, 23.3) * mm, v(24.08, 23.12) * mm, v(23.44, 22.98) * mm, v(22.65, 22.98) * mm]});
            skFitSpline(sketch, "E435", {"points": [v(22.65, 22.98) * mm, v(21.34, 22.98) * mm, v(21.22, 22.91) * mm, v(21.22, 22.18) * mm]});
            skFitSpline(sketch, "E436", {"points": [v(21.22, 22.18) * mm, v(21.22, 21.45) * mm, v(21.34, 21.39) * mm, v(22.65, 21.39) * mm]});
            skFitSpline(sketch, "E437", {"points": [v(22.65, 21.39) * mm, v(23.44, 21.39) * mm, v(24.08, 21.25) * mm, v(24.08, 21.07) * mm]});
            skFitSpline(sketch, "E438", {"points": [v(24.08, 21.07) * mm, v(24.08, 20.9) * mm, v(23.44, 20.75) * mm, v(22.65, 20.75) * mm]});
            skFitSpline(sketch, "E439", {"points": [v(22.65, 20.75) * mm, v(21.27, 20.75) * mm, v(21.22, 20.72) * mm, v(21.22, 19.8) * mm]});
            skFitSpline(sketch, "E440", {"points": [v(21.22, 19.8) * mm, v(21.22, 18.88) * mm, v(21.27, 18.85) * mm, v(22.65, 18.85) * mm]});
            skFitSpline(sketch, "E441", {"points": [v(22.65, 18.85) * mm, v(23.44, 18.85) * mm, v(24.08, 18.7) * mm, v(24.08, 18.53) * mm]});
            skFitSpline(sketch, "E442", {"points": [v(24.08, 18.53) * mm, v(24.08, 18.35) * mm, v(23.36, 18.21) * mm, v(22.5, 18.21) * mm]});
            skLineSegment(sketch, "E443", {"start": v(20.9, 20.91) * mm, "end": v(20.9, 23.61) * mm});
            skLineSegment(sketch, "E444", {"start": v(20.9, 23.61) * mm, "end": v(22.5, 23.61) * mm});
            skLineSegment(sketch, "E445", {"start": v(22.5, 23.61) * mm, "end": v(20.9, 20.91) * mm});
            skFitSpline(sketch, "E446", {"points": [v(26.54, 18.6) * mm, v(25.65, 19.28) * mm, v(25.29, 20.7) * mm, v(25.68, 21.91) * mm]});
            skFitSpline(sketch, "E447", {"points": [v(25.68, 21.91) * mm, v(26.63, 24.77) * mm, v(30.43, 23.94) * mm, v(30.43, 20.87) * mm]});
            skFitSpline(sketch, "E448", {"points": [v(30.43, 20.87) * mm, v(30.43, 18.73) * mm, v(28.13, 17.4) * mm, v(26.54, 18.6) * mm]});
            skLineSegment(sketch, "E449", {"start": v(22.5, 18.21) * mm, "end": v(20.9, 18.21) * mm});
            skLineSegment(sketch, "E450", {"start": v(20.9, 18.21) * mm, "end": v(20.9, 20.91) * mm});
            skLineSegment(sketch, "E451", {"start": v(20.9, 20.91) * mm, "end": v(22.5, 18.21) * mm});
            skFitSpline(sketch, "E452", {"points": [v(29.16, 19.16) * mm, v(30.46, 20.46) * mm, v(29.6, 23.3) * mm, v(27.92, 23.3) * mm]});
            skFitSpline(sketch, "E453", {"points": [v(27.92, 23.3) * mm, v(27.15, 23.3) * mm, v(25.99, 21.86) * mm, v(25.99, 20.91) * mm]});
            skFitSpline(sketch, "E454", {"points": [v(25.99, 20.91) * mm, v(25.99, 19.97) * mm, v(27.15, 18.53) * mm, v(27.92, 18.53) * mm]});
            skFitSpline(sketch, "E455", {"points": [v(27.92, 18.53) * mm, v(28.25, 18.53) * mm, v(28.81, 18.81) * mm, v(29.16, 19.16) * mm]});
            skFitSpline(sketch, "E456", {"points": [v(32.02, 20.73) * mm, v(32.02, 22.12) * mm, v(32.15, 23.34) * mm, v(32.31, 23.44) * mm]});
            skFitSpline(sketch, "E457", {"points": [v(32.31, 23.44) * mm, v(32.47, 23.53) * mm, v(33.37, 22.65) * mm, v(34.3, 21.48) * mm]});
            skFitSpline(sketch, "E458", {"points": [v(35.75, 18.86) * mm, v(35.36, 19.31) * mm, v(34.51, 20.31) * mm, v(33.86, 21.09) * mm]});
            skLineSegment(sketch, "E459", {"start": v(34.3, 21.48) * mm, "end": v(36, 19.34) * mm});
            skLineSegment(sketch, "E460", {"start": v(36, 19.34) * mm, "end": v(36.18, 21.56) * mm});
            skLineSegment(sketch, "E461", {"start": v(36.18, 21.56) * mm, "end": v(36.36, 23.77) * mm});
            skLineSegment(sketch, "E462", {"start": v(36.36, 23.77) * mm, "end": v(36.4, 20.91) * mm});
            skLineSegment(sketch, "E463", {"start": v(36.4, 20.91) * mm, "end": v(36.45, 18.05) * mm});
            skLineSegment(sketch, "E464", {"start": v(36.45, 18.05) * mm, "end": v(35.75, 18.86) * mm});
            skLineSegment(sketch, "E465", {"start": v(35.75, 18.86) * mm, "end": v(34.3, 21.48) * mm});
            skFitSpline(sketch, "E466", {"points": [v(32.67, 20.36) * mm, v(32.67, 19.15) * mm, v(32.52, 18.21) * mm, v(32.34, 18.21) * mm]});
            skFitSpline(sketch, "E467", {"points": [v(32.34, 18.21) * mm, v(32.16, 18.21) * mm, v(32.02, 19.26) * mm, v(32.02, 20.73) * mm]});
            skLineSegment(sketch, "E468", {"start": v(33.86, 21.09) * mm, "end": v(32.69, 22.5) * mm});
            skLineSegment(sketch, "E469", {"start": v(32.69, 22.5) * mm, "end": v(32.67, 20.36) * mm});
            skLineSegment(sketch, "E470", {"start": v(32.67, 20.36) * mm, "end": v(33.86, 21.09) * mm});
            skFitSpline(sketch, "E471", {"points": [v(40.29, 23.61) * mm, v(41.16, 23.61) * mm, v(41.87, 23.47) * mm, v(41.87, 23.3) * mm]});
            skFitSpline(sketch, "E472", {"points": [v(41.87, 23.3) * mm, v(41.87, 23.12) * mm, v(41.23, 22.98) * mm, v(40.44, 22.98) * mm]});
            skFitSpline(sketch, "E473", {"points": [v(40.44, 22.98) * mm, v(39.13, 22.98) * mm, v(39.01, 22.91) * mm, v(39.01, 22.18) * mm]});
            skFitSpline(sketch, "E474", {"points": [v(39.01, 22.18) * mm, v(39.01, 21.45) * mm, v(39.13, 21.39) * mm, v(40.44, 21.39) * mm]});
            skFitSpline(sketch, "E475", {"points": [v(40.44, 21.39) * mm, v(41.23, 21.39) * mm, v(41.87, 21.25) * mm, v(41.87, 21.07) * mm]});
            skFitSpline(sketch, "E476", {"points": [v(41.87, 21.07) * mm, v(41.87, 20.9) * mm, v(41.23, 20.75) * mm, v(40.44, 20.75) * mm]});
            skFitSpline(sketch, "E477", {"points": [v(40.44, 20.75) * mm, v(39.07, 20.75) * mm, v(39.01, 20.72) * mm, v(39.01, 19.8) * mm]});
            skFitSpline(sketch, "E478", {"points": [v(39.01, 19.8) * mm, v(39.01, 18.88) * mm, v(39.07, 18.85) * mm, v(40.44, 18.85) * mm]});
            skFitSpline(sketch, "E479", {"points": [v(40.44, 18.85) * mm, v(41.23, 18.85) * mm, v(41.87, 18.7) * mm, v(41.87, 18.53) * mm]});
            skFitSpline(sketch, "E480", {"points": [v(41.87, 18.53) * mm, v(41.87, 18.35) * mm, v(41.16, 18.21) * mm, v(40.29, 18.21) * mm]});
            skLineSegment(sketch, "E481", {"start": v(38.7, 20.91) * mm, "end": v(38.7, 23.61) * mm});
            skLineSegment(sketch, "E482", {"start": v(38.7, 23.61) * mm, "end": v(40.29, 23.61) * mm});
            skLineSegment(sketch, "E483", {"start": v(40.29, 23.61) * mm, "end": v(38.7, 20.91) * mm});
            skFitSpline(sketch, "E484", {"points": [v(-38.29, 32.9) * mm, v(-39.17, 33.58) * mm, v(-39.54, 35) * mm, v(-39.14, 36.21) * mm]});
            skFitSpline(sketch, "E485", {"points": [v(-39.14, 36.21) * mm, v(-38.2, 39.07) * mm, v(-34.4, 38.24) * mm, v(-34.4, 35.17) * mm]});
            skFitSpline(sketch, "E486", {"points": [v(-34.4, 35.17) * mm, v(-34.4, 33.03) * mm, v(-36.7, 31.7) * mm, v(-38.29, 32.9) * mm]});
            skLineSegment(sketch, "E487", {"start": v(40.29, 18.21) * mm, "end": v(38.7, 18.21) * mm});
            skLineSegment(sketch, "E488", {"start": v(38.7, 18.21) * mm, "end": v(38.7, 20.91) * mm});
            skLineSegment(sketch, "E489", {"start": v(38.7, 20.91) * mm, "end": v(40.29, 18.21) * mm});
            skFitSpline(sketch, "E490", {"points": [v(-35.66, 33.46) * mm, v(-34.37, 34.76) * mm, v(-35.23, 37.6) * mm, v(-36.9, 37.6) * mm]});
            skFitSpline(sketch, "E491", {"points": [v(-36.9, 37.6) * mm, v(-37.67, 37.6) * mm, v(-38.84, 36.16) * mm, v(-38.84, 35.21) * mm]});
            skFitSpline(sketch, "E492", {"points": [v(-38.84, 35.21) * mm, v(-38.84, 34.27) * mm, v(-37.67, 32.83) * mm, v(-36.9, 32.83) * mm]});
            skFitSpline(sketch, "E493", {"points": [v(-36.9, 32.83) * mm, v(-36.57, 32.83) * mm, v(-36.01, 33.11) * mm, v(-35.66, 33.46) * mm]});
            skFitSpline(sketch, "E494", {"points": [v(-32.8, 35.03) * mm, v(-32.8, 36.42) * mm, v(-32.67, 37.64) * mm, v(-32.51, 37.74) * mm]});
            skFitSpline(sketch, "E495", {"points": [v(-32.51, 37.74) * mm, v(-32.35, 37.83) * mm, v(-31.46, 36.95) * mm, v(-30.53, 35.78) * mm]});
            skFitSpline(sketch, "E496", {"points": [v(-29.08, 33.16) * mm, v(-29.47, 33.61) * mm, v(-30.31, 34.61) * mm, v(-30.96, 35.39) * mm]});
            skLineSegment(sketch, "E497", {"start": v(-30.53, 35.78) * mm, "end": v(-28.83, 33.64) * mm});
            skLineSegment(sketch, "E498", {"start": v(-28.83, 33.64) * mm, "end": v(-28.65, 35.86) * mm});
            skLineSegment(sketch, "E499", {"start": v(-28.65, 35.86) * mm, "end": v(-28.47, 38.07) * mm});
            skLineSegment(sketch, "E500", {"start": v(-28.47, 38.07) * mm, "end": v(-28.42, 35.21) * mm});
            skLineSegment(sketch, "E501", {"start": v(-28.42, 35.21) * mm, "end": v(-28.37, 32.35) * mm});
            skLineSegment(sketch, "E502", {"start": v(-28.37, 32.35) * mm, "end": v(-29.08, 33.16) * mm});
            skLineSegment(sketch, "E503", {"start": v(-29.08, 33.16) * mm, "end": v(-30.53, 35.78) * mm});
            skFitSpline(sketch, "E504", {"points": [v(-32.15, 34.66) * mm, v(-32.16, 33.45) * mm, v(-32.3, 32.51) * mm, v(-32.48, 32.51) * mm]});
            skFitSpline(sketch, "E505", {"points": [v(-32.48, 32.51) * mm, v(-32.67, 32.51) * mm, v(-32.8, 33.56) * mm, v(-32.8, 35.03) * mm]});
            skLineSegment(sketch, "E506", {"start": v(-30.96, 35.39) * mm, "end": v(-32.14, 36.8) * mm});
            skLineSegment(sketch, "E507", {"start": v(-32.14, 36.8) * mm, "end": v(-32.15, 34.66) * mm});
            skLineSegment(sketch, "E508", {"start": v(-32.15, 34.66) * mm, "end": v(-30.96, 35.39) * mm});
            skFitSpline(sketch, "E509", {"points": [v(-25.05, 32.97) * mm, v(-27.1, 33.86) * mm, v(-26.96, 36.81) * mm, v(-24.84, 37.55) * mm]});
            skFitSpline(sketch, "E510", {"points": [v(-24.84, 37.55) * mm, v(-23.57, 38) * mm, v(-22.95, 38.01) * mm, v(-22.95, 37.6) * mm]});
            skFitSpline(sketch, "E511", {"points": [v(-22.95, 37.6) * mm, v(-22.95, 37.42) * mm, v(-23.31, 37.28) * mm, v(-23.76, 37.28) * mm]});
            skFitSpline(sketch, "E512", {"points": [v(-23.76, 37.28) * mm, v(-24.9, 37.28) * mm, v(-26.23, 35.88) * mm, v(-25.96, 34.97) * mm]});
            skFitSpline(sketch, "E513", {"points": [v(-25.96, 34.97) * mm, v(-25.7, 34.07) * mm, v(-24.65, 33.15) * mm, v(-23.89, 33.15) * mm]});
            skFitSpline(sketch, "E514", {"points": [v(-23.89, 33.15) * mm, v(-23.57, 33.15) * mm, v(-23.22, 33) * mm, v(-23.1, 32.83) * mm]});
            skFitSpline(sketch, "E515", {"points": [v(-23.1, 32.83) * mm, v(-22.83, 32.38) * mm, v(-23.88, 32.45) * mm, v(-25.05, 32.97) * mm]});
            skFitSpline(sketch, "E516", {"points": [v(-19.77, 37.91) * mm, v(-18.9, 37.91) * mm, v(-18.18, 37.77) * mm, v(-18.18, 37.6) * mm]});
            skFitSpline(sketch, "E517", {"points": [v(-18.18, 37.6) * mm, v(-18.18, 37.42) * mm, v(-18.83, 37.28) * mm, v(-19.61, 37.28) * mm]});
            skFitSpline(sketch, "E518", {"points": [v(-19.61, 37.28) * mm, v(-20.93, 37.28) * mm, v(-21.04, 37.21) * mm, v(-21.04, 36.48) * mm]});
            skFitSpline(sketch, "E519", {"points": [v(-21.04, 36.48) * mm, v(-21.04, 35.75) * mm, v(-20.93, 35.69) * mm, v(-19.61, 35.69) * mm]});
            skFitSpline(sketch, "E520", {"points": [v(-19.61, 35.69) * mm, v(-18.83, 35.69) * mm, v(-18.18, 35.54) * mm, v(-18.18, 35.37) * mm]});
            skFitSpline(sketch, "E521", {"points": [v(-18.18, 35.37) * mm, v(-18.18, 35.2) * mm, v(-18.83, 35.05) * mm, v(-19.61, 35.05) * mm]});
            skFitSpline(sketch, "E522", {"points": [v(-19.61, 35.05) * mm, v(-21, 35.05) * mm, v(-21.04, 35.02) * mm, v(-21.04, 34.1) * mm]});
            skFitSpline(sketch, "E523", {"points": [v(-21.04, 34.1) * mm, v(-21.04, 33.18) * mm, v(-21, 33.15) * mm, v(-19.61, 33.15) * mm]});
            skFitSpline(sketch, "E524", {"points": [v(-19.61, 33.15) * mm, v(-18.83, 33.15) * mm, v(-18.18, 33) * mm, v(-18.18, 32.83) * mm]});
            skFitSpline(sketch, "E525", {"points": [v(-18.18, 32.83) * mm, v(-18.18, 32.65) * mm, v(-18.9, 32.51) * mm, v(-19.77, 32.51) * mm]});
            skLineSegment(sketch, "E526", {"start": v(-21.36, 35.21) * mm, "end": v(-21.36, 37.91) * mm});
            skLineSegment(sketch, "E527", {"start": v(-21.36, 37.91) * mm, "end": v(-19.77, 37.91) * mm});
            skLineSegment(sketch, "E528", {"start": v(-19.77, 37.91) * mm, "end": v(-21.36, 35.21) * mm});
            skFitSpline(sketch, "E529", {"points": [v(-14.37, 35.21) * mm, v(-14.37, 36.8) * mm, v(-14.24, 37.91) * mm, v(-14.05, 37.91) * mm]});
            skFitSpline(sketch, "E530", {"points": [v(-14.05, 37.91) * mm, v(-13.87, 37.91) * mm, v(-13.74, 36.8) * mm, v(-13.74, 35.21) * mm]});
            skFitSpline(sketch, "E531", {"points": [v(-13.74, 35.21) * mm, v(-13.74, 33.62) * mm, v(-13.87, 32.51) * mm, v(-14.05, 32.51) * mm]});
            skFitSpline(sketch, "E532", {"points": [v(-14.05, 32.51) * mm, v(-14.24, 32.51) * mm, v(-14.37, 33.62) * mm, v(-14.37, 35.21) * mm]});
            skLineSegment(sketch, "E533", {"start": v(-19.77, 32.51) * mm, "end": v(-21.36, 32.51) * mm});
            skLineSegment(sketch, "E534", {"start": v(-21.36, 32.51) * mm, "end": v(-21.36, 35.21) * mm});
            skLineSegment(sketch, "E535", {"start": v(-21.36, 35.21) * mm, "end": v(-19.77, 32.51) * mm});
            skFitSpline(sketch, "E536", {"points": [v(-11.83, 35.03) * mm, v(-11.83, 36.42) * mm, v(-11.7, 37.64) * mm, v(-11.54, 37.74) * mm]});
            skFitSpline(sketch, "E537", {"points": [v(-11.54, 37.74) * mm, v(-11.38, 37.83) * mm, v(-10.49, 36.95) * mm, v(-9.55, 35.78) * mm]});
            skFitSpline(sketch, "E538", {"points": [v(-8.1, 33.16) * mm, v(-8.5, 33.61) * mm, v(-9.34, 34.61) * mm, v(-9.99, 35.39) * mm]});
            skLineSegment(sketch, "E539", {"start": v(-9.55, 35.78) * mm, "end": v(-7.86, 33.64) * mm});
            skLineSegment(sketch, "E540", {"start": v(-7.86, 33.64) * mm, "end": v(-7.67, 35.86) * mm});
            skLineSegment(sketch, "E541", {"start": v(-7.67, 35.86) * mm, "end": v(-7.5, 38.07) * mm});
            skLineSegment(sketch, "E542", {"start": v(-7.5, 38.07) * mm, "end": v(-7.45, 35.21) * mm});
            skLineSegment(sketch, "E543", {"start": v(-7.45, 35.21) * mm, "end": v(-7.4, 32.35) * mm});
            skLineSegment(sketch, "E544", {"start": v(-7.4, 32.35) * mm, "end": v(-8.1, 33.16) * mm});
            skLineSegment(sketch, "E545", {"start": v(-8.1, 33.16) * mm, "end": v(-9.55, 35.78) * mm});
            skFitSpline(sketch, "E546", {"points": [v(-11.18, 34.66) * mm, v(-11.19, 33.45) * mm, v(-11.33, 32.51) * mm, v(-11.51, 32.51) * mm]});
            skFitSpline(sketch, "E547", {"points": [v(-11.51, 32.51) * mm, v(-11.7, 32.51) * mm, v(-11.83, 33.56) * mm, v(-11.83, 35.03) * mm]});
            skLineSegment(sketch, "E548", {"start": v(-9.99, 35.39) * mm, "end": v(-11.16, 36.8) * mm});
            skLineSegment(sketch, "E549", {"start": v(-11.16, 36.8) * mm, "end": v(-11.18, 34.66) * mm});
            skLineSegment(sketch, "E550", {"start": v(-11.18, 34.66) * mm, "end": v(-9.99, 35.39) * mm});
            skFitSpline(sketch, "E551", {"points": [v(-3.88, 32.81) * mm, v(-3.88, 33.37) * mm, v(-1.7, 37.91) * mm, v(-1.43, 37.91) * mm]});
            skFitSpline(sketch, "E552", {"points": [v(-1.43, 37.91) * mm, v(-1, 37.91) * mm, v(1.18, 32.85) * mm, v(0.85, 32.65) * mm]});
            skFitSpline(sketch, "E553", {"points": [v(0.85, 32.65) * mm, v(0.68, 32.55) * mm, v(0.4, 32.9) * mm, v(0.2, 33.44) * mm]});
            skFitSpline(sketch, "E554", {"points": [v(0.2, 33.44) * mm, v(-0.1, 34.33) * mm, v(-0.26, 34.42) * mm, v(-1.5, 34.42) * mm]});
            skFitSpline(sketch, "E555", {"points": [v(-1.5, 34.42) * mm, v(-2.74, 34.42) * mm, v(-2.9, 34.32) * mm, v(-3.2, 33.46) * mm]});
            skFitSpline(sketch, "E556", {"points": [v(-3.2, 33.46) * mm, v(-3.52, 32.54) * mm, v(-3.88, 32.2) * mm, v(-3.88, 32.81) * mm]});
            skFitSpline(sketch, "E557", {"points": [v(-0.7, 35.4) * mm, v(-0.7, 35.58) * mm, v(-0.87, 36.03) * mm, v(-1.06, 36.4) * mm]});
            skFitSpline(sketch, "E558", {"points": [v(-1.06, 36.4) * mm, v(-1.42, 37.06) * mm, v(-1.42, 37.06) * mm, v(-1.85, 36.3) * mm]});
            skFitSpline(sketch, "E559", {"points": [v(-1.85, 36.3) * mm, v(-2.45, 35.21) * mm, v(-2.4, 35.05) * mm, v(-1.5, 35.05) * mm]});
            skFitSpline(sketch, "E560", {"points": [v(-1.5, 35.05) * mm, v(-1.06, 35.05) * mm, v(-0.7, 35.2) * mm, v(-0.7, 35.4) * mm]});
            skFitSpline(sketch, "E561", {"points": [v(4.38, 35.21) * mm, v(4.38, 36.8) * mm, v(4.5, 37.91) * mm, v(4.7, 37.91) * mm]});
            skFitSpline(sketch, "E562", {"points": [v(4.7, 37.91) * mm, v(4.88, 37.91) * mm, v(5.01, 36.9) * mm, v(5.01, 35.53) * mm]});
            skFitSpline(sketch, "E563", {"points": [v(6.28, 33.15) * mm, v(6.98, 33.15) * mm, v(7.56, 33) * mm, v(7.56, 32.83) * mm]});
            skFitSpline(sketch, "E564", {"points": [v(7.56, 32.83) * mm, v(7.56, 32.65) * mm, v(6.84, 32.51) * mm, v(5.97, 32.51) * mm]});
            skLineSegment(sketch, "E565", {"start": v(5.01, 35.53) * mm, "end": v(5.01, 33.15) * mm});
            skLineSegment(sketch, "E566", {"start": v(5.01, 33.15) * mm, "end": v(6.28, 33.15) * mm});
            skLineSegment(sketch, "E567", {"start": v(6.28, 33.15) * mm, "end": v(5.01, 35.53) * mm});
            skFitSpline(sketch, "E568", {"points": [v(8.83, 35.21) * mm, v(8.83, 36.8) * mm, v(8.96, 37.91) * mm, v(9.14, 37.91) * mm]});
            skFitSpline(sketch, "E569", {"points": [v(9.14, 37.91) * mm, v(9.33, 37.91) * mm, v(9.46, 36.8) * mm, v(9.46, 35.21) * mm]});
            skFitSpline(sketch, "E570", {"points": [v(9.46, 35.21) * mm, v(9.46, 33.62) * mm, v(9.33, 32.51) * mm, v(9.14, 32.51) * mm]});
            skFitSpline(sketch, "E571", {"points": [v(9.14, 32.51) * mm, v(8.96, 32.51) * mm, v(8.83, 33.62) * mm, v(8.83, 35.21) * mm]});
            skLineSegment(sketch, "E572", {"start": v(5.97, 32.51) * mm, "end": v(4.38, 32.51) * mm});
            skLineSegment(sketch, "E573", {"start": v(4.38, 32.51) * mm, "end": v(4.38, 35.21) * mm});
            skLineSegment(sketch, "E574", {"start": v(4.38, 35.21) * mm, "end": v(5.97, 32.51) * mm});
            skFitSpline(sketch, "E575", {"points": [v(12.96, 37.91) * mm, v(13.83, 37.91) * mm, v(14.55, 37.77) * mm, v(14.55, 37.6) * mm]});
            skFitSpline(sketch, "E576", {"points": [v(14.55, 37.6) * mm, v(14.55, 37.42) * mm, v(13.97, 37.28) * mm, v(13.28, 37.28) * mm]});
            skFitSpline(sketch, "E577", {"points": [v(13.28, 37.28) * mm, v(12.08, 37.28) * mm, v(12, 37.22) * mm, v(12, 36.34) * mm]});
            skFitSpline(sketch, "E578", {"points": [v(12, 36.34) * mm, v(12, 35.47) * mm, v(12.1, 35.4) * mm, v(13.35, 35.28) * mm]});
            skLineSegment(sketch, "E579", {"start": v(11.37, 35.21) * mm, "end": v(11.37, 37.91) * mm});
            skLineSegment(sketch, "E580", {"start": v(11.37, 37.91) * mm, "end": v(12.96, 37.91) * mm});
            skLineSegment(sketch, "E581", {"start": v(12.96, 37.91) * mm, "end": v(11.37, 35.21) * mm});
            skFitSpline(sketch, "E582", {"points": [v(12, 33.78) * mm, v(12, 33.08) * mm, v(11.86, 32.51) * mm, v(11.69, 32.51) * mm]});
            skFitSpline(sketch, "E583", {"points": [v(11.69, 32.51) * mm, v(11.5, 32.51) * mm, v(11.37, 33.62) * mm, v(11.37, 35.21) * mm]});
            skLineSegment(sketch, "E584", {"start": v(13.35, 35.28) * mm, "end": v(14.7, 35.16) * mm});
            skLineSegment(sketch, "E585", {"start": v(14.7, 35.16) * mm, "end": v(13.35, 35.1) * mm});
            skLineSegment(sketch, "E586", {"start": v(13.35, 35.1) * mm, "end": v(12, 35.05) * mm});
            skLineSegment(sketch, "E587", {"start": v(12, 35.05) * mm, "end": v(12, 33.78) * mm});
            skLineSegment(sketch, "E588", {"start": v(12, 33.78) * mm, "end": v(13.35, 35.28) * mm});
            skFitSpline(sketch, "E589", {"points": [v(17.72, 37.91) * mm, v(18.6, 37.91) * mm, v(19.31, 37.77) * mm, v(19.31, 37.6) * mm]});
            skFitSpline(sketch, "E590", {"points": [v(19.31, 37.6) * mm, v(19.31, 37.42) * mm, v(18.67, 37.28) * mm, v(17.88, 37.28) * mm]});
            skFitSpline(sketch, "E591", {"points": [v(17.88, 37.28) * mm, v(16.57, 37.28) * mm, v(16.45, 37.21) * mm, v(16.45, 36.48) * mm]});
            skFitSpline(sketch, "E592", {"points": [v(16.45, 36.48) * mm, v(16.45, 35.75) * mm, v(16.57, 35.69) * mm, v(17.88, 35.69) * mm]});
            skFitSpline(sketch, "E593", {"points": [v(17.88, 35.69) * mm, v(18.67, 35.69) * mm, v(19.31, 35.54) * mm, v(19.31, 35.37) * mm]});
            skFitSpline(sketch, "E594", {"points": [v(19.31, 35.37) * mm, v(19.31, 35.2) * mm, v(18.67, 35.05) * mm, v(17.88, 35.05) * mm]});
            skFitSpline(sketch, "E595", {"points": [v(17.88, 35.05) * mm, v(16.5, 35.05) * mm, v(16.45, 35.02) * mm, v(16.45, 34.1) * mm]});
            skFitSpline(sketch, "E596", {"points": [v(16.45, 34.1) * mm, v(16.45, 33.18) * mm, v(16.5, 33.15) * mm, v(17.88, 33.15) * mm]});
            skFitSpline(sketch, "E597", {"points": [v(17.88, 33.15) * mm, v(18.67, 33.15) * mm, v(19.31, 33) * mm, v(19.31, 32.83) * mm]});
            skFitSpline(sketch, "E598", {"points": [v(19.31, 32.83) * mm, v(19.31, 32.65) * mm, v(18.6, 32.51) * mm, v(17.72, 32.51) * mm]});
            skLineSegment(sketch, "E599", {"start": v(16.13, 35.21) * mm, "end": v(16.13, 37.91) * mm});
            skLineSegment(sketch, "E600", {"start": v(16.13, 37.91) * mm, "end": v(17.72, 37.91) * mm});
            skLineSegment(sketch, "E601", {"start": v(17.72, 37.91) * mm, "end": v(16.13, 35.21) * mm});
            skLineSegment(sketch, "E602", {"start": v(17.72, 32.51) * mm, "end": v(16.13, 32.51) * mm});
            skLineSegment(sketch, "E603", {"start": v(16.13, 32.51) * mm, "end": v(16.13, 35.21) * mm});
            skLineSegment(sketch, "E604", {"start": v(16.13, 35.21) * mm, "end": v(17.72, 32.51) * mm});
            skFitSpline(sketch, "E605", {"points": [v(21.22, 37.28) * mm, v(20.7, 37.28) * mm, v(20.27, 37.42) * mm, v(20.27, 37.6) * mm]});
            skFitSpline(sketch, "E606", {"points": [v(20.27, 37.6) * mm, v(20.27, 37.78) * mm, v(21.22, 37.91) * mm, v(22.5, 37.91) * mm]});
            skFitSpline(sketch, "E607", {"points": [v(22.5, 37.91) * mm, v(23.76, 37.91) * mm, v(24.71, 37.78) * mm, v(24.71, 37.6) * mm]});
            skFitSpline(sketch, "E608", {"points": [v(24.71, 37.6) * mm, v(24.71, 37.42) * mm, v(24.29, 37.28) * mm, v(23.76, 37.28) * mm]});
            skLineSegment(sketch, "E609", {"start": v(22.17, 34.9) * mm, "end": v(22.17, 37.28) * mm});
            skLineSegment(sketch, "E610", {"start": v(22.17, 37.28) * mm, "end": v(21.22, 37.28) * mm});
            skLineSegment(sketch, "E611", {"start": v(21.22, 37.28) * mm, "end": v(22.17, 34.9) * mm});
            skFitSpline(sketch, "E612", {"points": [v(22.8, 34.9) * mm, v(22.8, 33.52) * mm, v(22.67, 32.51) * mm, v(22.5, 32.51) * mm]});
            skFitSpline(sketch, "E613", {"points": [v(22.5, 32.51) * mm, v(22.3, 32.51) * mm, v(22.17, 33.52) * mm, v(22.17, 34.9) * mm]});
            skLineSegment(sketch, "E614", {"start": v(23.76, 37.28) * mm, "end": v(22.8, 37.28) * mm});
            skLineSegment(sketch, "E615", {"start": v(22.8, 37.28) * mm, "end": v(22.8, 34.9) * mm});
            skLineSegment(sketch, "E616", {"start": v(22.8, 34.9) * mm, "end": v(23.76, 37.28) * mm});
            skFitSpline(sketch, "E617", {"points": [v(25.67, 35.21) * mm, v(25.67, 36.8) * mm, v(25.8, 37.91) * mm, v(25.99, 37.91) * mm]});
            skFitSpline(sketch, "E618", {"points": [v(25.99, 37.91) * mm, v(26.17, 37.91) * mm, v(26.3, 36.8) * mm, v(26.3, 35.21) * mm]});
            skFitSpline(sketch, "E619", {"points": [v(26.3, 35.21) * mm, v(26.3, 33.62) * mm, v(26.17, 32.51) * mm, v(25.99, 32.51) * mm]});
            skFitSpline(sketch, "E620", {"points": [v(25.99, 32.51) * mm, v(25.8, 32.51) * mm, v(25.67, 33.62) * mm, v(25.67, 35.21) * mm]});
            skFitSpline(sketch, "E621", {"points": [v(28, 33.23) * mm, v(28.09, 33.62) * mm, v(28.34, 34.83) * mm, v(28.55, 35.93) * mm]});
            skFitSpline(sketch, "E622", {"points": [v(28.55, 35.93) * mm, v(28.76, 37.02) * mm, v(29.06, 37.91) * mm, v(29.23, 37.91) * mm]});
            skFitSpline(sketch, "E623", {"points": [v(29.23, 37.91) * mm, v(29.4, 37.91) * mm, v(29.91, 37.05) * mm, v(30.38, 36) * mm]});
            skFitSpline(sketch, "E624", {"points": [v(30.38, 36) * mm, v(30.84, 34.96) * mm, v(31.3, 34.1) * mm, v(31.39, 34.1) * mm]});
            skFitSpline(sketch, "E625", {"points": [v(31.39, 34.1) * mm, v(31.48, 34.1) * mm, v(31.93, 34.96) * mm, v(32.4, 36) * mm]});
            skFitSpline(sketch, "E626", {"points": [v(32.4, 36) * mm, v(32.86, 37.05) * mm, v(33.37, 37.91) * mm, v(33.52, 37.91) * mm]});
            skFitSpline(sketch, "E627", {"points": [v(33.52, 37.91) * mm, v(33.81, 37.91) * mm, v(34.92, 32.78) * mm, v(34.7, 32.54) * mm]});
            skFitSpline(sketch, "E628", {"points": [v(34.7, 32.54) * mm, v(34.43, 32.26) * mm, v(34.21, 32.81) * mm, v(33.86, 34.7) * mm]});
            skFitSpline(sketch, "E629", {"points": [v(33.86, 34.7) * mm, v(33.66, 35.76) * mm, v(33.4, 36.64) * mm, v(33.3, 36.64) * mm]});
            skFitSpline(sketch, "E630", {"points": [v(33.3, 36.64) * mm, v(33.19, 36.64) * mm, v(32.77, 35.85) * mm, v(32.36, 34.88) * mm]});
            skFitSpline(sketch, "E631", {"points": [v(32.36, 34.88) * mm, v(31.96, 33.9) * mm, v(31.5, 33.16) * mm, v(31.35, 33.21) * mm]});
            skFitSpline(sketch, "E632", {"points": [v(31.35, 33.21) * mm, v(31.2, 33.26) * mm, v(30.66, 34.16) * mm, v(30.16, 35.21) * mm]});
            skFitSpline(sketch, "E633", {"points": [v(28.84, 34.81) * mm, v(28.61, 33.55) * mm, v(28.3, 32.51) * mm, v(28.12, 32.51) * mm]});
            skFitSpline(sketch, "E634", {"points": [v(28.12, 32.51) * mm, v(27.96, 32.51) * mm, v(27.9, 32.83) * mm, v(28, 33.23) * mm]});
            skLineSegment(sketch, "E635", {"start": v(30.16, 35.21) * mm, "end": v(29.26, 37.12) * mm});
            skLineSegment(sketch, "E636", {"start": v(29.26, 37.12) * mm, "end": v(28.84, 34.81) * mm});
            skLineSegment(sketch, "E637", {"start": v(28.84, 34.81) * mm, "end": v(30.16, 35.21) * mm});
            skFitSpline(sketch, "E638", {"points": [v(37.74, 37.91) * mm, v(38.62, 37.91) * mm, v(39.33, 37.77) * mm, v(39.33, 37.6) * mm]});
            skFitSpline(sketch, "E639", {"points": [v(39.33, 37.6) * mm, v(39.33, 37.42) * mm, v(38.76, 37.28) * mm, v(38.06, 37.28) * mm]});
            skFitSpline(sketch, "E640", {"points": [v(38.06, 37.28) * mm, v(36.92, 37.28) * mm, v(36.8, 37.2) * mm, v(36.8, 36.48) * mm]});
            skFitSpline(sketch, "E641", {"points": [v(36.8, 36.48) * mm, v(36.8, 35.77) * mm, v(36.92, 35.69) * mm, v(38.06, 35.69) * mm]});
            skFitSpline(sketch, "E642", {"points": [v(38.06, 35.69) * mm, v(38.76, 35.69) * mm, v(39.33, 35.54) * mm, v(39.33, 35.37) * mm]});
            skFitSpline(sketch, "E643", {"points": [v(39.33, 35.37) * mm, v(39.33, 35.2) * mm, v(38.76, 35.05) * mm, v(38.06, 35.05) * mm]});
            skFitSpline(sketch, "E644", {"points": [v(38.06, 35.05) * mm, v(36.86, 35.05) * mm, v(36.8, 35) * mm, v(36.8, 34.1) * mm]});
            skFitSpline(sketch, "E645", {"points": [v(36.8, 34.1) * mm, v(36.8, 33.2) * mm, v(36.86, 33.15) * mm, v(38.04, 33.15) * mm]});
            skFitSpline(sketch, "E646", {"points": [v(38.04, 33.15) * mm, v(38.73, 33.15) * mm, v(39.38, 33) * mm, v(39.5, 32.83) * mm]});
            skFitSpline(sketch, "E647", {"points": [v(39.5, 32.83) * mm, v(39.61, 32.63) * mm, v(39.02, 32.51) * mm, v(37.92, 32.51) * mm]});
            skLineSegment(sketch, "E648", {"start": v(36.15, 35.21) * mm, "end": v(36.15, 37.91) * mm});
            skLineSegment(sketch, "E649", {"start": v(36.15, 37.91) * mm, "end": v(37.74, 37.91) * mm});
            skLineSegment(sketch, "E650", {"start": v(37.74, 37.91) * mm, "end": v(36.15, 35.21) * mm});
            skLineSegment(sketch, "E651", {"start": v(37.92, 32.51) * mm, "end": v(36.15, 32.51) * mm});
            skLineSegment(sketch, "E652", {"start": v(36.15, 32.51) * mm, "end": v(36.15, 35.21) * mm});
            skLineSegment(sketch, "E653", {"start": v(36.15, 35.21) * mm, "end": v(37.92, 32.51) * mm});
            skSolve(sketch);
        }
        {
            var Q0;
            Q0=makeQuery(id+"F4.imprint","IMPRINT",FACE,{"disambiguationData":[TD([[makeQuery(id+"F4.imprint","IMPRINT",EDGE,{"derivedFrom":sQuery(id+"F4.wireOp",EDGE,"E484")}),-1.0]])]});
            var Q1;
            Q1=makeQuery(id+"F4.imprint","IMPRINT",FACE,{"disambiguationData":[TD([[makeQuery(id+"F4.imprint","IMPRINT",EDGE,{"derivedFrom":sQuery(id+"F4.wireOp",EDGE,"E494")}),-1.0]])]});
            var Q2;
            Q2=makeQuery(id+"F4.imprint","IMPRINT",FACE,{"disambiguationData":[TD([[makeQuery(id+"F4.imprint","IMPRINT",EDGE,{"derivedFrom":sQuery(id+"F4.wireOp",EDGE,"E497")}),-1.0]])]});
            var Q3;
            Q3=makeQuery(id+"F4.imprint","IMPRINT",FACE,{"disambiguationData":[TD([[makeQuery(id+"F4.imprint","IMPRINT",EDGE,{"derivedFrom":sQuery(id+"F4.wireOp",EDGE,"E509")}),-1.0]])]});
            var Q4;
            {var subQ8=sQuery(id+"F4.wireOp",EDGE,"E520");Q4=makeQuery(id+"F4.imprint","IMPRINT",FACE,{"disambiguationData":[TD([[makeQuery(id+"F4.imprint","IMPRINT",EDGE,{"derivedFrom":subQ8}),-1.0]])]});}
            var Q5;
            {var subQ6=sQuery(id+"F4.wireOp",EDGE,"E526");Q5=makeQuery(id+"F4.imprint","IMPRINT",FACE,{"disambiguationData":[TD([[makeQuery(id+"F4.imprint","IMPRINT",EDGE,{"derivedFrom":subQ6}),-1.0]])]});}
            var Q6;
            {var subQ0=sQuery(id+"F4.wireOp",EDGE,"E516");Q6=makeQuery(id+"F4.imprint","IMPRINT",FACE,{"disambiguationData":[TD([[makeQuery(id+"F4.imprint","IMPRINT",EDGE,{"derivedFrom":subQ0}),-1.0]])]});}
            var Q7;
            {var subQ0=sQuery(id+"F4.wireOp",EDGE,"E533");Q7=makeQuery(id+"F4.imprint","IMPRINT",FACE,{"disambiguationData":[TD([[makeQuery(id+"F4.imprint","IMPRINT",EDGE,{"derivedFrom":subQ0}),-1.0]])]});}
            var Q8;
            {var subQ0=sQuery(id+"F4.wireOp",EDGE,"E524");Q8=makeQuery(id+"F4.imprint","IMPRINT",FACE,{"disambiguationData":[TD([[makeQuery(id+"F4.imprint","IMPRINT",EDGE,{"derivedFrom":subQ0}),-1.0]])]});}
            var Q9;
            Q9=makeQuery(id+"F4.imprint","IMPRINT",FACE,{"disambiguationData":[TD([[makeQuery(id+"F4.imprint","IMPRINT",EDGE,{"derivedFrom":sQuery(id+"F4.wireOp",EDGE,"E529")}),-1.0]])]});
            var Q10;
            Q10=makeQuery(id+"F4.imprint","IMPRINT",FACE,{"disambiguationData":[TD([[makeQuery(id+"F4.imprint","IMPRINT",EDGE,{"derivedFrom":sQuery(id+"F4.wireOp",EDGE,"E536")}),-1.0]])]});
            var Q11;
            Q11=makeQuery(id+"F4.imprint","IMPRINT",FACE,{"disambiguationData":[TD([[makeQuery(id+"F4.imprint","IMPRINT",EDGE,{"derivedFrom":sQuery(id+"F4.wireOp",EDGE,"E539")}),-1.0]])]});
            var Q12;
            Q12=makeQuery(id+"F4.imprint","IMPRINT",FACE,{"disambiguationData":[TD([[makeQuery(id+"F4.imprint","IMPRINT",EDGE,{"derivedFrom":sQuery(id+"F4.wireOp",EDGE,"E551")}),-1.0]])]});
            var Q13;
            {var subQ1=sQuery(id+"F4.wireOp",EDGE,"E572");Q13=makeQuery(id+"F4.imprint","IMPRINT",FACE,{"disambiguationData":[TD([[makeQuery(id+"F4.imprint","IMPRINT",EDGE,{"derivedFrom":subQ1}),-1.0]])]});}
            var Q14;
            {var subQ0=sQuery(id+"F4.wireOp",EDGE,"E561");Q14=makeQuery(id+"F4.imprint","IMPRINT",FACE,{"disambiguationData":[TD([[makeQuery(id+"F4.imprint","IMPRINT",EDGE,{"derivedFrom":subQ0}),-1.0]])]});}
            var Q15;
            {var subQ0=sQuery(id+"F4.wireOp",EDGE,"E563");Q15=makeQuery(id+"F4.imprint","IMPRINT",FACE,{"disambiguationData":[TD([[makeQuery(id+"F4.imprint","IMPRINT",EDGE,{"derivedFrom":subQ0}),-1.0]])]});}
            var Q16;
            Q16=makeQuery(id+"F4.imprint","IMPRINT",FACE,{"disambiguationData":[TD([[makeQuery(id+"F4.imprint","IMPRINT",EDGE,{"derivedFrom":sQuery(id+"F4.wireOp",EDGE,"E568")}),-1.0]])]});
            var Q17;
            Q17=makeQuery(id+"F4.imprint","IMPRINT",FACE,{"disambiguationData":[TD([[makeQuery(id+"F4.imprint","IMPRINT",EDGE,{"derivedFrom":sQuery(id+"F4.wireOp",EDGE,"E582")}),-1.0]])]});
            var Q18;
            {var subQ1=sQuery(id+"F4.wireOp",EDGE,"E579");Q18=makeQuery(id+"F4.imprint","IMPRINT",FACE,{"disambiguationData":[TD([[makeQuery(id+"F4.imprint","IMPRINT",EDGE,{"derivedFrom":subQ1}),-1.0]])]});}
            var Q19;
            {var subQ0=sQuery(id+"F4.wireOp",EDGE,"E575");Q19=makeQuery(id+"F4.imprint","IMPRINT",FACE,{"disambiguationData":[TD([[makeQuery(id+"F4.imprint","IMPRINT",EDGE,{"derivedFrom":subQ0}),-1.0]])]});}
            var Q20;
            {var subQ6=sQuery(id+"F4.wireOp",EDGE,"E599");Q20=makeQuery(id+"F4.imprint","IMPRINT",FACE,{"disambiguationData":[TD([[makeQuery(id+"F4.imprint","IMPRINT",EDGE,{"derivedFrom":subQ6}),-1.0]])]});}
            var Q21;
            {var subQ0=sQuery(id+"F4.wireOp",EDGE,"E589");Q21=makeQuery(id+"F4.imprint","IMPRINT",FACE,{"disambiguationData":[TD([[makeQuery(id+"F4.imprint","IMPRINT",EDGE,{"derivedFrom":subQ0}),-1.0]])]});}
            var Q22;
            {var subQ8=sQuery(id+"F4.wireOp",EDGE,"E593");Q22=makeQuery(id+"F4.imprint","IMPRINT",FACE,{"disambiguationData":[TD([[makeQuery(id+"F4.imprint","IMPRINT",EDGE,{"derivedFrom":subQ8}),-1.0]])]});}
            var Q23;
            {var subQ7=sQuery(id+"F4.wireOp",EDGE,"E602");Q23=makeQuery(id+"F4.imprint","IMPRINT",FACE,{"disambiguationData":[TD([[makeQuery(id+"F4.imprint","IMPRINT",EDGE,{"derivedFrom":subQ7}),-1.0]])]});}
            var Q24;
            {var subQ0=sQuery(id+"F4.wireOp",EDGE,"E597");Q24=makeQuery(id+"F4.imprint","IMPRINT",FACE,{"disambiguationData":[TD([[makeQuery(id+"F4.imprint","IMPRINT",EDGE,{"derivedFrom":subQ0}),-1.0]])]});}
            var Q25;
            Q25=makeQuery(id+"F4.imprint","IMPRINT",FACE,{"disambiguationData":[TD([[makeQuery(id+"F4.imprint","IMPRINT",EDGE,{"derivedFrom":sQuery(id+"F4.wireOp",EDGE,"E605")}),-1.0]])]});
            var Q26;
            Q26=makeQuery(id+"F4.imprint","IMPRINT",FACE,{"disambiguationData":[TD([[makeQuery(id+"F4.imprint","IMPRINT",EDGE,{"derivedFrom":sQuery(id+"F4.wireOp",EDGE,"E617")}),-1.0]])]});
            var Q27;
            Q27=makeQuery(id+"F4.imprint","IMPRINT",FACE,{"disambiguationData":[TD([[makeQuery(id+"F4.imprint","IMPRINT",EDGE,{"derivedFrom":sQuery(id+"F4.wireOp",EDGE,"E621")}),-1.0]])]});
            var Q28;
            {var subQ8=sQuery(id+"F4.wireOp",EDGE,"E642");Q28=makeQuery(id+"F4.imprint","IMPRINT",FACE,{"disambiguationData":[TD([[makeQuery(id+"F4.imprint","IMPRINT",EDGE,{"derivedFrom":subQ8}),-1.0]])]});}
            var Q29;
            {var subQ6=sQuery(id+"F4.wireOp",EDGE,"E648");Q29=makeQuery(id+"F4.imprint","IMPRINT",FACE,{"disambiguationData":[TD([[makeQuery(id+"F4.imprint","IMPRINT",EDGE,{"derivedFrom":subQ6}),-1.0]])]});}
            var Q30;
            {var subQ7=sQuery(id+"F4.wireOp",EDGE,"E651");Q30=makeQuery(id+"F4.imprint","IMPRINT",FACE,{"disambiguationData":[TD([[makeQuery(id+"F4.imprint","IMPRINT",EDGE,{"derivedFrom":subQ7}),-1.0]])]});}
            var Q31;
            {var subQ0=sQuery(id+"F4.wireOp",EDGE,"E646");Q31=makeQuery(id+"F4.imprint","IMPRINT",FACE,{"disambiguationData":[TD([[makeQuery(id+"F4.imprint","IMPRINT",EDGE,{"derivedFrom":subQ0}),-1.0]])]});}
            var Q32;
            {var subQ0=sQuery(id+"F4.wireOp",EDGE,"E638");Q32=makeQuery(id+"F4.imprint","IMPRINT",FACE,{"disambiguationData":[TD([[makeQuery(id+"F4.imprint","IMPRINT",EDGE,{"derivedFrom":subQ0}),-1.0]])]});}
            var Q33;
            Q33=makeQuery(id+"F4.imprint","IMPRINT",FACE,{"disambiguationData":[TD([[makeQuery(id+"F4.imprint","IMPRINT",EDGE,{"derivedFrom":sQuery(id+"F4.wireOp",EDGE,"E314")}),-1.0]])]});
            var Q34;
            Q34=makeQuery(id+"F4.imprint","IMPRINT",FACE,{"disambiguationData":[TD([[makeQuery(id+"F4.imprint","IMPRINT",EDGE,{"derivedFrom":sQuery(id+"F4.wireOp",EDGE,"E325")}),-1.0]])]});
            var Q35;
            Q35=makeQuery(id+"F4.imprint","IMPRINT",FACE,{"disambiguationData":[TD([[makeQuery(id+"F4.imprint","IMPRINT",EDGE,{"derivedFrom":sQuery(id+"F4.wireOp",EDGE,"E322")}),-1.0]])]});
            var Q36;
            Q36=makeQuery(id+"F4.imprint","IMPRINT",FACE,{"disambiguationData":[TD([[makeQuery(id+"F4.imprint","IMPRINT",EDGE,{"derivedFrom":sQuery(id+"F4.wireOp",EDGE,"E333")}),-1.0]])]});
            var Q37;
            Q37=makeQuery(id+"F4.imprint","IMPRINT",FACE,{"disambiguationData":[TD([[makeQuery(id+"F4.imprint","IMPRINT",EDGE,{"derivedFrom":sQuery(id+"F4.wireOp",EDGE,"E344")}),-1.0]])]});
            var Q38;
            {var subQ8=sQuery(id+"F4.wireOp",EDGE,"E363");Q38=makeQuery(id+"F4.imprint","IMPRINT",FACE,{"disambiguationData":[TD([[makeQuery(id+"F4.imprint","IMPRINT",EDGE,{"derivedFrom":subQ8}),-1.0]])]});}
            var Q39;
            {var subQ6=sQuery(id+"F4.wireOp",EDGE,"E369");Q39=makeQuery(id+"F4.imprint","IMPRINT",FACE,{"disambiguationData":[TD([[makeQuery(id+"F4.imprint","IMPRINT",EDGE,{"derivedFrom":subQ6}),-1.0]])]});}
            var Q40;
            {var subQ0=sQuery(id+"F4.wireOp",EDGE,"E359");Q40=makeQuery(id+"F4.imprint","IMPRINT",FACE,{"disambiguationData":[TD([[makeQuery(id+"F4.imprint","IMPRINT",EDGE,{"derivedFrom":subQ0}),-1.0]])]});}
            var Q41;
            {var subQ7=sQuery(id+"F4.wireOp",EDGE,"E372");Q41=makeQuery(id+"F4.imprint","IMPRINT",FACE,{"disambiguationData":[TD([[makeQuery(id+"F4.imprint","IMPRINT",EDGE,{"derivedFrom":subQ7}),-1.0]])]});}
            var Q42;
            {var subQ0=sQuery(id+"F4.wireOp",EDGE,"E367");Q42=makeQuery(id+"F4.imprint","IMPRINT",FACE,{"disambiguationData":[TD([[makeQuery(id+"F4.imprint","IMPRINT",EDGE,{"derivedFrom":subQ0}),-1.0]])]});}
            var Q43;
            {var subQ7=sQuery(id+"F4.wireOp",EDGE,"E388");Q43=makeQuery(id+"F4.imprint","IMPRINT",FACE,{"disambiguationData":[TD([[makeQuery(id+"F4.imprint","IMPRINT",EDGE,{"derivedFrom":subQ7}),-1.0]])]});}
            var Q44;
            {var subQ8=sQuery(id+"F4.wireOp",EDGE,"E379");Q44=makeQuery(id+"F4.imprint","IMPRINT",FACE,{"disambiguationData":[TD([[makeQuery(id+"F4.imprint","IMPRINT",EDGE,{"derivedFrom":subQ8}),-1.0]])]});}
            var Q45;
            {var subQ6=sQuery(id+"F4.wireOp",EDGE,"E385");Q45=makeQuery(id+"F4.imprint","IMPRINT",FACE,{"disambiguationData":[TD([[makeQuery(id+"F4.imprint","IMPRINT",EDGE,{"derivedFrom":subQ6}),-1.0]])]});}
            var Q46;
            {var subQ0=sQuery(id+"F4.wireOp",EDGE,"E375");Q46=makeQuery(id+"F4.imprint","IMPRINT",FACE,{"disambiguationData":[TD([[makeQuery(id+"F4.imprint","IMPRINT",EDGE,{"derivedFrom":subQ0}),-1.0]])]});}
            var Q47;
            {var subQ0=sQuery(id+"F4.wireOp",EDGE,"E383");Q47=makeQuery(id+"F4.imprint","IMPRINT",FACE,{"disambiguationData":[TD([[makeQuery(id+"F4.imprint","IMPRINT",EDGE,{"derivedFrom":subQ0}),-1.0]])]});}
            var Q48;
            Q48=makeQuery(id+"F4.imprint","IMPRINT",FACE,{"disambiguationData":[TD([[makeQuery(id+"F4.imprint","IMPRINT",EDGE,{"derivedFrom":sQuery(id+"F4.wireOp",EDGE,"E391")}),-1.0]])]});
            var Q49;
            {var subQ0=sQuery(id+"F4.wireOp",EDGE,"E408");Q49=makeQuery(id+"F4.imprint","IMPRINT",FACE,{"disambiguationData":[TD([[makeQuery(id+"F4.imprint","IMPRINT",EDGE,{"derivedFrom":subQ0}),-1.0]])]});}
            var Q50;
            Q50=makeQuery(id+"F4.imprint","IMPRINT",FACE,{"disambiguationData":[TD([[makeQuery(id+"F4.imprint","IMPRINT",EDGE,{"derivedFrom":sQuery(id+"F4.wireOp",EDGE,"E398")}),-1.0]])]});
            var Q51;
            Q51=makeQuery(id+"F4.imprint","IMPRINT",FACE,{"disambiguationData":[TD([[makeQuery(id+"F4.imprint","IMPRINT",EDGE,{"derivedFrom":sQuery(id+"F4.wireOp",EDGE,"E411")}),-1.0]])]});
            var Q52;
            Q52=makeQuery(id+"F4.imprint","IMPRINT",FACE,{"disambiguationData":[TD([[makeQuery(id+"F4.imprint","IMPRINT",EDGE,{"derivedFrom":sQuery(id+"F4.wireOp",EDGE,"E418")}),-1.0]])]});
            var Q53;
            {var subQ6=sQuery(id+"F4.wireOp",EDGE,"E443");Q53=makeQuery(id+"F4.imprint","IMPRINT",FACE,{"disambiguationData":[TD([[makeQuery(id+"F4.imprint","IMPRINT",EDGE,{"derivedFrom":subQ6}),-1.0]])]});}
            var Q54;
            {var subQ8=sQuery(id+"F4.wireOp",EDGE,"E437");Q54=makeQuery(id+"F4.imprint","IMPRINT",FACE,{"disambiguationData":[TD([[makeQuery(id+"F4.imprint","IMPRINT",EDGE,{"derivedFrom":subQ8}),-1.0]])]});}
            var Q55;
            {var subQ1=sQuery(id+"F4.wireOp",EDGE,"E449");Q55=makeQuery(id+"F4.imprint","IMPRINT",FACE,{"disambiguationData":[TD([[makeQuery(id+"F4.imprint","IMPRINT",EDGE,{"derivedFrom":subQ1}),-1.0]])]});}
            var Q56;
            {var subQ0=sQuery(id+"F4.wireOp",EDGE,"E441");Q56=makeQuery(id+"F4.imprint","IMPRINT",FACE,{"disambiguationData":[TD([[makeQuery(id+"F4.imprint","IMPRINT",EDGE,{"derivedFrom":subQ0}),-1.0]])]});}
            var Q57;
            {var subQ0=sQuery(id+"F4.wireOp",EDGE,"E433");Q57=makeQuery(id+"F4.imprint","IMPRINT",FACE,{"disambiguationData":[TD([[makeQuery(id+"F4.imprint","IMPRINT",EDGE,{"derivedFrom":subQ0}),-1.0]])]});}
            var Q58;
            Q58=makeQuery(id+"F4.imprint","IMPRINT",FACE,{"disambiguationData":[TD([[makeQuery(id+"F4.imprint","IMPRINT",EDGE,{"derivedFrom":sQuery(id+"F4.wireOp",EDGE,"E446")}),-1.0]])]});
            var Q59;
            Q59=makeQuery(id+"F4.imprint","IMPRINT",FACE,{"disambiguationData":[TD([[makeQuery(id+"F4.imprint","IMPRINT",EDGE,{"derivedFrom":sQuery(id+"F4.wireOp",EDGE,"E456")}),-1.0]])]});
            var Q60;
            Q60=makeQuery(id+"F4.imprint","IMPRINT",FACE,{"disambiguationData":[TD([[makeQuery(id+"F4.imprint","IMPRINT",EDGE,{"derivedFrom":sQuery(id+"F4.wireOp",EDGE,"E459")}),-1.0]])]});
            var Q61;
            {var subQ1=sQuery(id+"F4.wireOp",EDGE,"E487");Q61=makeQuery(id+"F4.imprint","IMPRINT",FACE,{"disambiguationData":[TD([[makeQuery(id+"F4.imprint","IMPRINT",EDGE,{"derivedFrom":subQ1}),-1.0]])]});}
            var Q62;
            {var subQ8=sQuery(id+"F4.wireOp",EDGE,"E475");Q62=makeQuery(id+"F4.imprint","IMPRINT",FACE,{"disambiguationData":[TD([[makeQuery(id+"F4.imprint","IMPRINT",EDGE,{"derivedFrom":subQ8}),-1.0]])]});}
            var Q63;
            {var subQ6=sQuery(id+"F4.wireOp",EDGE,"E481");Q63=makeQuery(id+"F4.imprint","IMPRINT",FACE,{"disambiguationData":[TD([[makeQuery(id+"F4.imprint","IMPRINT",EDGE,{"derivedFrom":subQ6}),-1.0]])]});}
            var Q64;
            {var subQ0=sQuery(id+"F4.wireOp",EDGE,"E471");Q64=makeQuery(id+"F4.imprint","IMPRINT",FACE,{"disambiguationData":[TD([[makeQuery(id+"F4.imprint","IMPRINT",EDGE,{"derivedFrom":subQ0}),-1.0]])]});}
            var Q65;
            {var subQ0=sQuery(id+"F4.wireOp",EDGE,"E479");Q65=makeQuery(id+"F4.imprint","IMPRINT",FACE,{"disambiguationData":[TD([[makeQuery(id+"F4.imprint","IMPRINT",EDGE,{"derivedFrom":subQ0}),-1.0]])]});}
            var Q66;
            Q66=makeQuery(id+"F4.imprint","IMPRINT",FACE,{"disambiguationData":[TD([[makeQuery(id+"F4.imprint","IMPRINT",EDGE,{"derivedFrom":sQuery(id+"F4.wireOp",EDGE,"E185")}),-1.0]])]});
            var Q67;
            Q67=makeQuery(id+"F4.imprint","IMPRINT",FACE,{"disambiguationData":[TD([[makeQuery(id+"F4.imprint","IMPRINT",EDGE,{"derivedFrom":sQuery(id+"F4.wireOp",EDGE,"E204")}),-1.0]])]});
            var Q68;
            Q68=makeQuery(id+"F4.imprint","IMPRINT",FACE,{"disambiguationData":[TD([[makeQuery(id+"F4.imprint","IMPRINT",EDGE,{"derivedFrom":sQuery(id+"F4.wireOp",EDGE,"E222")}),-1.0]])]});
            var Q69;
            Q69=makeQuery(id+"F4.imprint","IMPRINT",FACE,{"disambiguationData":[TD([[makeQuery(id+"F4.imprint","IMPRINT",EDGE,{"derivedFrom":sQuery(id+"F4.wireOp",EDGE,"E229")}),-1.0]])]});
            var Q70;
            Q70=makeQuery(id+"F4.imprint","IMPRINT",FACE,{"disambiguationData":[TD([[makeQuery(id+"F4.imprint","IMPRINT",EDGE,{"derivedFrom":sQuery(id+"F4.wireOp",EDGE,"E236")}),-1.0]])]});
            var Q71;
            Q71=makeQuery(id+"F4.imprint","IMPRINT",FACE,{"disambiguationData":[TD([[makeQuery(id+"F4.imprint","IMPRINT",EDGE,{"derivedFrom":sQuery(id+"F4.wireOp",EDGE,"E252")}),-1.0]])]});
            var Q72;
            Q72=makeQuery(id+"F4.imprint","IMPRINT",FACE,{"disambiguationData":[TD([[makeQuery(id+"F4.imprint","IMPRINT",EDGE,{"derivedFrom":sQuery(id+"F4.wireOp",EDGE,"E262")}),-1.0]])]});
            var Q73;
            Q73=makeQuery(id+"F4.imprint","IMPRINT",FACE,{"disambiguationData":[TD([[makeQuery(id+"F4.imprint","IMPRINT",EDGE,{"derivedFrom":sQuery(id+"F4.wireOp",EDGE,"E265")}),-1.0]])]});
            var Q74;
            Q74=makeQuery(id+"F4.imprint","IMPRINT",FACE,{"disambiguationData":[TD([[makeQuery(id+"F4.imprint","IMPRINT",EDGE,{"derivedFrom":sQuery(id+"F4.wireOp",EDGE,"E277")}),-1.0]])]});
            var Q75;
            {var subQ1=sQuery(id+"F4.wireOp",EDGE,"E311");Q75=makeQuery(id+"F4.imprint","IMPRINT",FACE,{"disambiguationData":[TD([[makeQuery(id+"F4.imprint","IMPRINT",EDGE,{"derivedFrom":subQ1}),-1.0]])]});}
            var Q76;
            {var subQ8=sQuery(id+"F4.wireOp",EDGE,"E294");Q76=makeQuery(id+"F4.imprint","IMPRINT",FACE,{"disambiguationData":[TD([[makeQuery(id+"F4.imprint","IMPRINT",EDGE,{"derivedFrom":subQ8}),-1.0]])]});}
            var Q77;
            {var subQ6=sQuery(id+"F4.wireOp",EDGE,"E300");Q77=makeQuery(id+"F4.imprint","IMPRINT",FACE,{"disambiguationData":[TD([[makeQuery(id+"F4.imprint","IMPRINT",EDGE,{"derivedFrom":subQ6}),-1.0]])]});}
            var Q78;
            {var subQ0=sQuery(id+"F4.wireOp",EDGE,"E290");Q78=makeQuery(id+"F4.imprint","IMPRINT",FACE,{"disambiguationData":[TD([[makeQuery(id+"F4.imprint","IMPRINT",EDGE,{"derivedFrom":subQ0}),-1.0]])]});}
            var Q79;
            {var subQ0=sQuery(id+"F4.wireOp",EDGE,"E298");Q79=makeQuery(id+"F4.imprint","IMPRINT",FACE,{"disambiguationData":[TD([[makeQuery(id+"F4.imprint","IMPRINT",EDGE,{"derivedFrom":subQ0}),-1.0]])]});}
            var Q80;
            Q80=makeQuery(id+"F4.imprint","IMPRINT",FACE,{"disambiguationData":[TD([[makeQuery(id+"F4.imprint","IMPRINT",EDGE,{"derivedFrom":sQuery(id+"F4.wireOp",EDGE,"E303")}),-1.0]])]});
            var Q81;
            Q81=makeQuery(id+"F4.imprint","IMPRINT",FACE,{"disambiguationData":[TD([[makeQuery(id+"F4.imprint","IMPRINT",EDGE,{"derivedFrom":sQuery(id+"F4.wireOp",EDGE,"E42")}),-1.0]])]});
            var Q82;
            Q82=makeQuery(id+"F4.imprint","IMPRINT",FACE,{"disambiguationData":[TD([[makeQuery(id+"F4.imprint","IMPRINT",EDGE,{"derivedFrom":sQuery(id+"F4.wireOp",EDGE,"E174")}),-1.0]])]});
            var Q83;
            Q83=makeQuery(id+"F4.imprint","IMPRINT",FACE,{"disambiguationData":[TD([[makeQuery(id+"F4.imprint","IMPRINT",EDGE,{"derivedFrom":sQuery(id+"F4.wireOp",EDGE,"E178")}),-1.0]])]});
            var Q84;
            Q84=makeQuery(id+"F4.imprint","IMPRINT",FACE,{"disambiguationData":[TD([[makeQuery(id+"F4.imprint","IMPRINT",EDGE,{"derivedFrom":sQuery(id+"F4.wireOp",EDGE,"E84")}),-1.0]])]});
            var Q85;
            Q85=makeQuery(id+"F4.imprint","IMPRINT",FACE,{"disambiguationData":[TD([[makeQuery(id+"F4.imprint","IMPRINT",EDGE,{"derivedFrom":sQuery(id+"F4.wireOp",EDGE,"E153")}),-1.0]])]});
            var Q86;
            Q86=makeQuery(id+"F4.imprint","IMPRINT",FACE,{"disambiguationData":[TD([[makeQuery(id+"F4.imprint","IMPRINT",EDGE,{"derivedFrom":sQuery(id+"F4.wireOp",EDGE,"E158")}),-1.0]])]});
            var Q87;
            Q87=makeQuery(id+"F4.imprint","IMPRINT",FACE,{"disambiguationData":[TD([[makeQuery(id+"F4.imprint","IMPRINT",EDGE,{"derivedFrom":sQuery(id+"F4.wireOp",EDGE,"E90")}),-1.0]])]});
            var Q88;
            Q88=makeQuery(id+"F4.imprint","IMPRINT",FACE,{"disambiguationData":[TD([[makeQuery(id+"F4.imprint","IMPRINT",EDGE,{"derivedFrom":sQuery(id+"F4.wireOp",EDGE,"E93")}),-1.0]])]});
            var Q89;
            Q89=makeQuery(id+"F4.imprint","IMPRINT",FACE,{"disambiguationData":[TD([[makeQuery(id+"F4.imprint","IMPRINT",EDGE,{"derivedFrom":sQuery(id+"F4.wireOp",EDGE,"E163")}),-1.0]])]});
            var Q90;
            Q90=makeQuery(id+"F4.imprint","IMPRINT",FACE,{"disambiguationData":[TD([[makeQuery(id+"F4.imprint","IMPRINT",EDGE,{"derivedFrom":sQuery(id+"F4.wireOp",EDGE,"E99")}),-1.0]])]});
            var Q91;
            Q91=makeQuery(id+"F4.imprint","IMPRINT",FACE,{"disambiguationData":[TD([[makeQuery(id+"F4.imprint","IMPRINT",EDGE,{"derivedFrom":sQuery(id+"F4.wireOp",EDGE,"E167")}),-1.0]])]});
            var Q92;
            Q92=makeQuery(id+"F4.imprint","IMPRINT",FACE,{"disambiguationData":[TD([[makeQuery(id+"F4.imprint","IMPRINT",EDGE,{"derivedFrom":sQuery(id+"F4.wireOp",EDGE,"E142")}),-1.0]])]});
            var Q93;
            Q93=makeQuery(id+"F4.imprint","IMPRINT",FACE,{"disambiguationData":[TD([[makeQuery(id+"F4.imprint","IMPRINT",EDGE,{"derivedFrom":sQuery(id+"F4.wireOp",EDGE,"E148")}),-1.0]])]});
            var Q94;
            Q94=makeQuery(id+"F4.imprint","IMPRINT",FACE,{"disambiguationData":[TD([[makeQuery(id+"F4.imprint","IMPRINT",EDGE,{"derivedFrom":sQuery(id+"F4.wireOp",EDGE,"E13")}),-1.0]])]});
            var Q95;
            Q95=makeQuery(id+"F4.imprint","IMPRINT",FACE,{"disambiguationData":[TD([[makeQuery(id+"F4.imprint","IMPRINT",EDGE,{"derivedFrom":sQuery(id+"F4.wireOp",EDGE,"E34")}),-1.0]])]});
            var Q96;
            Q96=makeQuery(id+"F4.imprint","IMPRINT",FACE,{"disambiguationData":[TD([[makeQuery(id+"F4.imprint","IMPRINT",EDGE,{"derivedFrom":sQuery(id+"F4.wireOp",EDGE,"E102")}),-1.0]])]});
            var Q97;
            Q97=makeQuery(id+"F4.imprint","IMPRINT",FACE,{"disambiguationData":[TD([[makeQuery(id+"F4.imprint","IMPRINT",EDGE,{"derivedFrom":sQuery(id+"F4.wireOp",EDGE,"E112")}),-1.0]])]});
            var Q98;
            Q98=makeQuery(id+"F4.imprint","IMPRINT",FACE,{"disambiguationData":[TD([[makeQuery(id+"F4.imprint","IMPRINT",EDGE,{"derivedFrom":sQuery(id+"F4.wireOp",EDGE,"E62")}),-1.0]])]});
            var Q99;
            Q99=makeQuery(id+"F4.imprint","IMPRINT",FACE,{"disambiguationData":[TD([[makeQuery(id+"F4.imprint","IMPRINT",EDGE,{"derivedFrom":sQuery(id+"F4.wireOp",EDGE,"E181")}),-1.0]])]});
            var Q100;
            Q100=makeQuery(id+"F4.imprint","IMPRINT",FACE,{"disambiguationData":[TD([[makeQuery(id+"F4.imprint","IMPRINT",EDGE,{"derivedFrom":sQuery(id+"F4.wireOp",EDGE,"E170")}),-1.0]])]});
            var Q101;
            Q101=makeQuery(id+"F4.imprint","IMPRINT",FACE,{"disambiguationData":[TD([[makeQuery(id+"F4.imprint","IMPRINT",EDGE,{"derivedFrom":sQuery(id+"F4.wireOp",EDGE,"E120")}),-1.0]])]});
            var Q102;
            Q102=makeQuery(id+"F4.imprint","IMPRINT",FACE,{"disambiguationData":[TD([[makeQuery(id+"F4.imprint","IMPRINT",EDGE,{"derivedFrom":sQuery(id+"F4.wireOp",EDGE,"E125")}),-1.0]])]});
            var Q103;
            Q103=makeQuery(id+"F4.imprint","IMPRINT",FACE,{"disambiguationData":[TD([[makeQuery(id+"F4.imprint","IMPRINT",EDGE,{"derivedFrom":sQuery(id+"F4.wireOp",EDGE,"E73")}),-1.0]])]});
            var Q104;
            Q104=makeQuery(id+"F4.imprint","IMPRINT",FACE,{"disambiguationData":[TD([[makeQuery(id+"F4.imprint","IMPRINT",EDGE,{"derivedFrom":sQuery(id+"F4.wireOp",EDGE,"E80")}),-1.0]])]});
            var Q105;
            Q105=makeQuery(id+"F4.imprint","IMPRINT",FACE,{"disambiguationData":[TD([[makeQuery(id+"F4.imprint","IMPRINT",EDGE,{"derivedFrom":sQuery(id+"F4.wireOp",EDGE,"E22")}),-1.0]])]});
            var Q106;
            Q106=makeQuery(id+"F4.imprint","IMPRINT",FACE,{"disambiguationData":[TD([[makeQuery(id+"F4.imprint","IMPRINT",EDGE,{"derivedFrom":sQuery(id+"F4.wireOp",EDGE,"E2")}),-1.0]])]});
            var Q107;
            Q107=makeQuery(id+"F4.imprint","IMPRINT",FACE,{"disambiguationData":[TD([[makeQuery(id+"F4.imprint","IMPRINT",EDGE,{"derivedFrom":sQuery(id+"F4.wireOp",EDGE,"E133")}),-1.0]])]});
            var Q108;
            Q108=makeQuery(id+"F4.imprint","IMPRINT",FACE,{"disambiguationData":[TD([[makeQuery(id+"F4.imprint","IMPRINT",EDGE,{"derivedFrom":sQuery(id+"F4.wireOp",EDGE,"E136")}),-1.0]])]});
            var Q109;
            Q109=makeQuery(id+"F4.imprint","IMPRINT",FACE,{"disambiguationData":[TD([[makeQuery(id+"F4.imprint","IMPRINT",EDGE,{"derivedFrom":sQuery(id+"F4.wireOp",EDGE,"E139")}),-1.0]])]});
            extrude(context, id + "F5", {"entities" : qUnion([Q0, Q1, Q2, Q3, Q4, Q5, Q6, Q7, Q8, Q9, Q10, Q11, Q12, Q13, Q14, Q15, Q16, Q17, Q18, Q19, Q20, Q21, Q22, Q23, Q24, Q25, Q26, Q27, Q28, Q29, Q30, Q31, Q32, Q33, Q34, Q35, Q36, Q37, Q38, Q39, Q40, Q41, Q42, Q43, Q44, Q45, Q46, Q47, Q48, Q49, Q50, Q51, Q52, Q53, Q54, Q55, Q56, Q57, Q58, Q59, Q60, Q61, Q62, Q63, Q64, Q65, Q66, Q67, Q68, Q69, Q70, Q71, Q72, Q73, Q74, Q75, Q76, Q77, Q78, Q79, Q80, Q81, Q82, Q83, Q84, Q85, Q86, Q87, Q88, Q89, Q90, Q91, Q92, Q93, Q94, Q95, Q96, Q97, Q98, Q99, Q100, Q101, Q102, Q103, Q104, Q105, Q106, Q107, Q108, Q109]), "operationType" : NewBodyOperationType.REMOVE, "flatOperationType" : FlatOperationType.REMOVE, "oppositeDirection" : true, "depth" : 5 * mm, "offsetDistance" : 25 * mm, "domain" : OperationDomain.MODEL});
        }
    });
